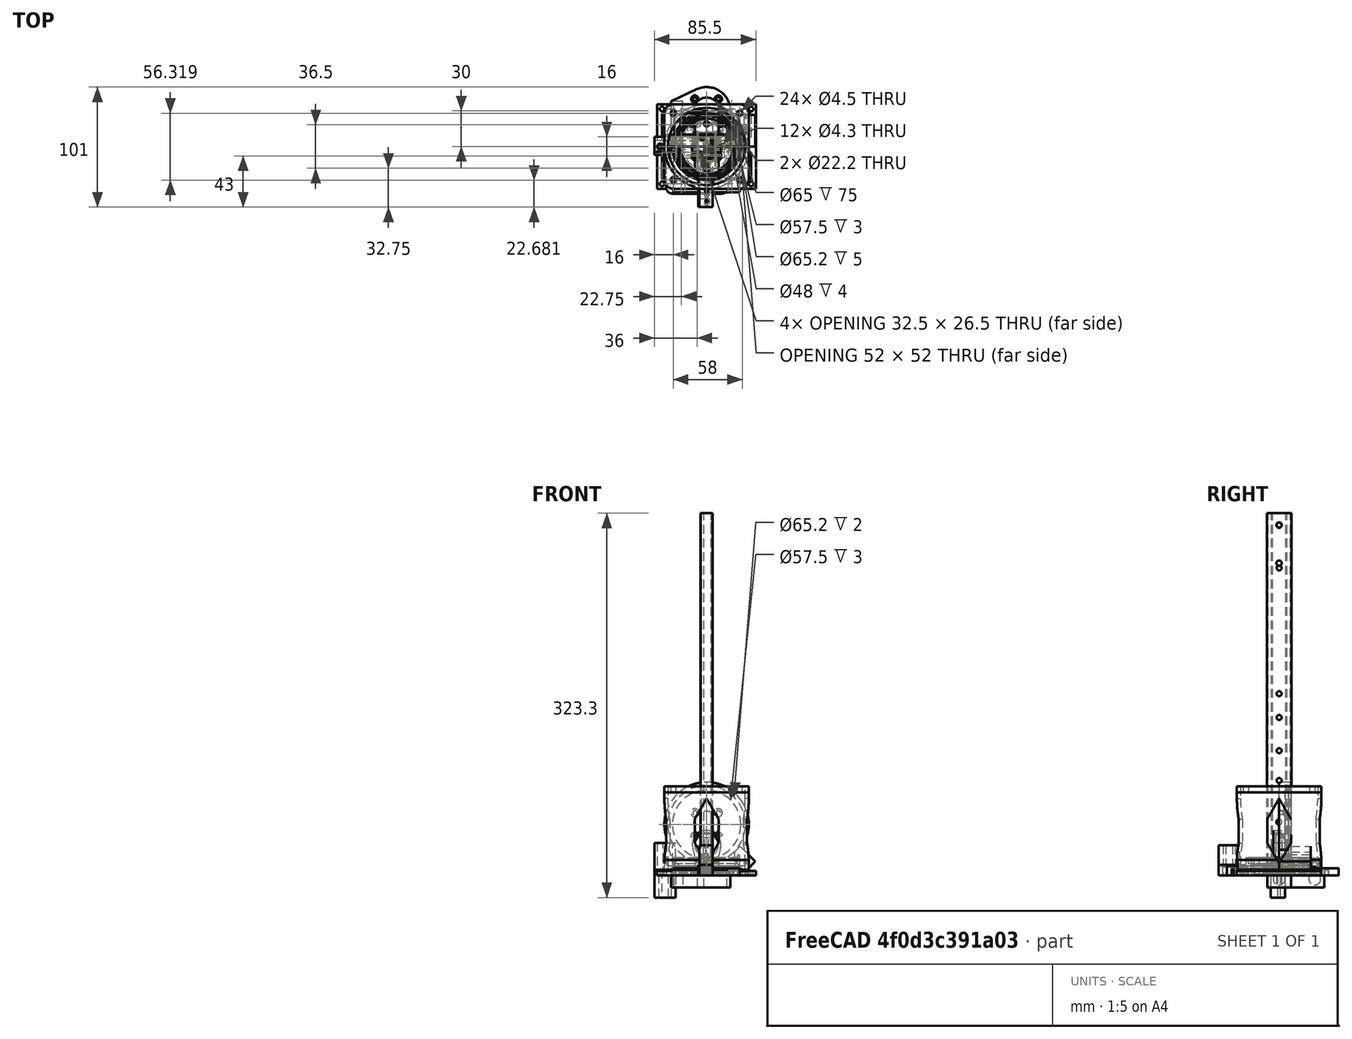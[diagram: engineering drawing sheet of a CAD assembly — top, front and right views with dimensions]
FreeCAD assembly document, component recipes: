
FREECAD ASSEMBLY — COMPONENT RECIPES ("A4")

This assembly document has 19 components, labeled P0..P18 below (a component is one placed body or linked part). 19 of them carry a construction recipe — the FreeCAD feature program that regenerates the part from scratch, quoted from this document or its linked companion documents; the rest are supplied as boundary geometry only. No exploded tour is included for this assembly.
COMPONENT P0 — recipe-attached ("J2_CABLE_GUIDE_1V0", modeled in this document).
Construction recipe (the document's own serialized feature program — sketch geometry with constraints, then the solid features built on it; lengths are millimeters unless a unit is written):

FEATURE [PartDesign::CoordinateSystem] LCS_0012
  AttacherType = Attacher::AttachEngine3D
  MapMode = 2
  Support = -> [X_Axis032]
FEATURE [Sketcher::SketchObject] Sketch067
  FullyConstrained = true
  MapMode = 5
  Support = -> [XY_Plane032]
  sketch-geometry (6):
    g0: Circle CenterX=0 CenterY=19 CenterZ=0 NormalX=0 NormalY=0 NormalZ=1 AngleXU=0 Radius=2.25
    g1: Circle CenterX=0 CenterY=-19 CenterZ=0 NormalX=0 NormalY=0 NormalZ=1 AngleXU=0 Radius=2.25
    g2: ArcOfCircle CenterX=0 CenterY=0 CenterZ=0 NormalX=0 NormalY=0 NormalZ=1 AngleXU=0 Radius=23.5 StartAngle=1.13125 EndAngle=2.01035
    g3: ArcOfCircle CenterX=0 CenterY=0 CenterZ=0 NormalX=0 NormalY=0 NormalZ=1 AngleXU=0 Radius=23.5 StartAngle=4.27284 EndAngle=5.15194
    g4: LineSegment StartX=-10 StartY=21.2662 StartZ=0 EndX=-10 EndY=-21.2662 EndZ=0
    g5: LineSegment StartX=10 StartY=-21.2662 StartZ=0 EndX=10 EndY=21.2662 EndZ=0
  constraints (16):
    c: PointOnObject(g0,g-2)
    c: Diameter(g1) = 4.5
    c: Equal(g1,g0)
    c: DistanceY(g1,g0) = 38
    c: Symmetric(g0,g1,g-1)
    c: Coincident(g2,g-1)
    c: Coincident(g3,g2)
    c: Coincident(g4,g3)
    c: Coincident(g5,g3)
    c: Coincident(g5,g2)
    c: Coincident(g2,g4)
    c: Vertical(g4)
    c: Symmetric(g2,g3,g-1)
    c: Horizontal(g2,g2)
    c: DistanceX(g2,g2) = 20
    c: Diameter(g2) = 47
FEATURE [PartDesign::Pad] Pad043
  Direction = (1,1,1)
  Length = 15
  Length2 = 100
  Profile = -> Sketch067
  Type = 0
FEATURE [Sketcher::SketchObject] Sketch068
  FullyConstrained = true
  MapMode = 5
  Placement = pos=(0,0,0) rot=(1,0,0;1.5708rad)
  Support = -> [XZ_Plane032]
  sketch-geometry (5):
    g0: Circle CenterX=0 CenterY=26 CenterZ=0 NormalX=0 NormalY=0 NormalZ=1 AngleXU=0 Radius=10
    g1: ArcOfCircle CenterX=0 CenterY=26 CenterZ=0 NormalX=0 NormalY=0 NormalZ=1 AngleXU=0 Radius=12 StartAngle=6.08159 EndAngle=9.62637
    g2: LineSegment StartX=-11.757 StartY=23.5973 StartZ=0 EndX=-10 EndY=15 EndZ=0
    g3: LineSegment StartX=11.757 StartY=23.5973 StartZ=0 EndX=10 EndY=15 EndZ=0
    g4: LineSegment StartX=10 StartY=15 StartZ=0 EndX=-10 EndY=15 EndZ=0
  constraints (12):
    c: PointOnObject(g0,g-2)
    c: Diameter(g0) = 20
    c: Coincident(g1,g0)
    c: Coincident(g4,g3)
    c: Coincident(g4,g2)
    c: Symmetric(g2,g3,g-2)
    c: DistanceX(g4,g4) = 20
    c: DistanceY(g-1,g3) = 15
    c: Diameter(g1) = 24
    c: DistanceY(g-1,g0) = 26
    c: Tangent(g2,g1) = -1.5708
    c: Tangent(g3,g1) = 1.5708
FEATURE [PartDesign::Pad] Pad044
  BaseFeature = -> Pad043
  Direction = (1,1,1)
  Length = 10
  Length2 = 100
  Midplane = true
  Profile = -> Sketch068
  Type = 0
FEATURE [Sketcher::SketchObject] Sketch069
  FullyConstrained = true
  MapMode = 5
  Placement = pos=(0,0,0) rot=(0.57735,0.57735,0.57735;2.0944rad)
  Support = -> [YZ_Plane032]
  expr: Constraints[9] = <<var>>.humerusW + 2
  sketch-geometry (4):
    g0: LineSegment StartX=-11.3187 StartY=0 StartZ=0 EndX=11.3187 EndY=0 EndZ=0
    g1: LineSegment StartX=11.3187 StartY=0 StartZ=0 EndX=11.3187 EndY=11 EndZ=0
    g2: LineSegment StartX=11.3187 StartY=11 StartZ=0 EndX=-11.3187 EndY=11 EndZ=0
    g3: LineSegment StartX=-11.3187 StartY=11 StartZ=0 EndX=-11.3187 EndY=0 EndZ=0
  constraints (11):
    c: Coincident(g0,g1)
    c: Coincident(g1,g2)
    c: Coincident(g2,g3)
    c: Coincident(g3,g0)
    c: Horizontal(g0)
    c: Vertical(g1)
    c: Vertical(g3)
    c: PointOnObject(g0,g-1)
    c: Symmetric(g2,g1,g-2)
    c: DistanceX(g2,g2) = 22.6375
    c: DistanceY(g1,g1) = 11
FEATURE [PartDesign::Pocket] Pocket022
  BaseFeature = -> Pad044
  Length = 5
  Length2 = 100
  Midplane = true
  Profile = -> Sketch069
  Type = 1
FEATURE [PartDesign::Body] J2_CABLE_GUIDE_1_0  label="Body008"
  Group = -> [LCS_0012,Sketch067,Pad043,Sketch068,Pad044,Sketch069,Pocket022]
  Origin = -> Origin032
  Tip = -> Pocket022
COMPONENT P1 — recipe-attached ("J0_BASE_2V0", modeled in this document).
Construction recipe (the document's own serialized feature program — sketch geometry with constraints, then the solid features built on it; lengths are millimeters unless a unit is written):

FEATURE [Sketcher::SketchObject] Sketch004
  FullyConstrained = true
  MapMode = 5
  Support = -> [XY_Plane004]
  expr: Constraints[46] = <<var>>.motorJ0HoleD
  expr: Constraints[41] = <<var>>.motorJ0LocD
  expr: Constraints[40] = <<var>>.motorJ0HolePD
  expr: Constraints[24] = <<var>>.riserOD
  expr: Constraints[20] = <<var>>.riserOD - 15
  expr: Constraints[16] = <<var>>.riserHoleD
  sketch-geometry (22):
    g0: LineSegment StartX=-28 StartY=35.5 StartZ=0 EndX=28 EndY=35.5 EndZ=0
    g1: LineSegment StartX=35.5 StartY=28 StartZ=0 EndX=35.5 EndY=-28 EndZ=0
    g2: LineSegment StartX=28 StartY=-35.5 StartZ=0 EndX=-28 EndY=-35.5 EndZ=0
    g3: LineSegment StartX=-35.5 StartY=-28 StartZ=0 EndX=-35.5 EndY=28 EndZ=0
    g4: ArcOfCircle CenterX=-28 CenterY=28 CenterZ=0 NormalX=0 NormalY=0 NormalZ=1 AngleXU=0 Radius=7.5 StartAngle=1.5708 EndAngle=3.14159
    g5: ArcOfCircle CenterX=-28 CenterY=-28 CenterZ=0 NormalX=0 NormalY=0 NormalZ=1 AngleXU=0 Radius=7.5 StartAngle=3.14159 EndAngle=4.71239
    g6: ArcOfCircle CenterX=28 CenterY=-28 CenterZ=0 NormalX=0 NormalY=0 NormalZ=1 AngleXU=0 Radius=7.5 StartAngle=4.71239 EndAngle=6.28319
    g7: ArcOfCircle CenterX=28 CenterY=28 CenterZ=0 NormalX=0 NormalY=0 NormalZ=1 AngleXU=0 Radius=7.5 StartAngle=-9e-16 EndAngle=1.5708
    g8: Circle CenterX=-28 CenterY=28 CenterZ=0 NormalX=0 NormalY=0 NormalZ=1 AngleXU=0 Radius=2.25
    g9: Circle CenterX=28 CenterY=28 CenterZ=0 NormalX=0 NormalY=0 NormalZ=1 AngleXU=0 Radius=2.25
    g10: Circle CenterX=28 CenterY=-28 CenterZ=0 NormalX=0 NormalY=0 NormalZ=1 AngleXU=0 Radius=2.25
    g11: Circle CenterX=-28 CenterY=-28 CenterZ=0 NormalX=0 NormalY=0 NormalZ=1 AngleXU=0 Radius=2.25
    g12: Circle CenterX=0 CenterY=0 CenterZ=0 NormalX=0 NormalY=0 NormalZ=1 AngleXU=0 Radius=11.1
    g13: LineSegment StartX=-9.89949 StartY=9.89949 StartZ=0 EndX=9.89949 EndY=9.89949 EndZ=0
    g14: LineSegment StartX=9.89949 StartY=9.89949 StartZ=0 EndX=9.89949 EndY=-9.89949 EndZ=0
    g15: LineSegment StartX=9.89949 StartY=-9.89949 StartZ=0 EndX=-9.89949 EndY=-9.89949 EndZ=0
    g16: LineSegment StartX=-9.89949 StartY=-9.89949 StartZ=0 EndX=-9.89949 EndY=9.89949 EndZ=0
    g17: Circle CenterX=0 CenterY=0 CenterZ=0 NormalX=0 NormalY=0 NormalZ=1 AngleXU=0 Radius=14
    g18: Circle CenterX=-9.89949 CenterY=9.89949 CenterZ=0 NormalX=0 NormalY=0 NormalZ=1 AngleXU=0 Radius=1.65
    g19: Circle CenterX=9.89949 CenterY=9.89949 CenterZ=0 NormalX=0 NormalY=0 NormalZ=1 AngleXU=0 Radius=1.65
    g20: Circle CenterX=9.89949 CenterY=-9.89949 CenterZ=0 NormalX=0 NormalY=0 NormalZ=1 AngleXU=0 Radius=1.65
    g21: Circle CenterX=-9.89949 CenterY=-9.89949 CenterZ=0 NormalX=0 NormalY=0 NormalZ=1 AngleXU=0 Radius=1.65
  constraints (50):
    c: Horizontal(g0)
    c: Horizontal(g2)
    c: Vertical(g1)
    c: Vertical(g3)
    c: Tangent(g0,g4) = 1.5708
    c: Tangent(g3,g4) = 1.5708
    c: Tangent(g3,g5) = 1.5708
    c: Tangent(g2,g5) = 1.5708
    c: Tangent(g2,g6) = 1.5708
    c: Tangent(g1,g6) = 1.5708
    c: Tangent(g1,g7) = 1.5708
    c: Tangent(g0,g7) = 1.5708
    c: Coincident(g8,g4)
    c: Coincident(g9,g7)
    c: Coincident(g10,g6)
    c: Coincident(g11,g5)
    c: Diameter(g11) = 4.5
    c: Equal(g11,g8)
    c: Equal(g11,g9)
    c: Equal(g11,g10)
    c: DistanceX(g4,g7) = 56
    c: Symmetric(g4,g5,g-1)
    c: Symmetric(g4,g7,g-2)
    c: Equal(g0,g3)
    c: DistanceX(g3,g1) = 71
    c: Equal(g6,g7)
    c: Coincident(g12,g-1)
    c: Coincident(g13,g14)
    c: Coincident(g14,g15)
    c: Coincident(g15,g16)
    c: Coincident(g16,g13)
    c: Horizontal(g13)
    c: Horizontal(g15)
    c: Vertical(g14)
    c: Vertical(g16)
    c: Coincident(g17,g12)
    c: PointOnObject(g13,g17)
    c: PointOnObject(g13,g17)
    c: Equal(g14,g15)
    c: PointOnObject(g14,g17)
    c: Diameter(g17) = 28
    c: Diameter(g12) = 22.2
    c: Coincident(g18,g13)
    c: Coincident(g19,g13)
    c: Coincident(g20,g14)
    c: Coincident(g21,g15)
    c: Diameter(g21) = 3.3
    c: Equal(g21,g20)
    c: Equal(g21,g19)
    c: Equal(g21,g18)
FEATURE [PartDesign::Pad] Pad005
  Direction = (1,1,1)
  Length = 5
  Length2 = 100
  Profile = -> Sketch004
  Refine = true
  Type = 0
FEATURE [Sketcher::SketchObject] Sketch005
  AttachmentOffset = pos=(0,0,5) rot=(0,0,1;0rad)
  FullyConstrained = true
  MapMode = 5
  Placement = pos=(0,0,5) rot=(0,0,1;0rad)
  Support = -> [XY_Plane004]
  expr: .AttachmentOffset.Base.z = 5
  sketch-geometry (2):
    g0: Circle CenterX=0 CenterY=0 CenterZ=0 NormalX=0 NormalY=0 NormalZ=1 AngleXU=0 Radius=35.5
    g1: Circle CenterX=0 CenterY=0 CenterZ=0 NormalX=0 NormalY=0 NormalZ=1 AngleXU=0 Radius=32.6
  constraints (4):
    c: Coincident(g0,g-1)
    c: Coincident(g1,g0)
    c: Diameter(g1) = 65.2
    c: Diameter(g0) = 71
FEATURE [PartDesign::Pad] Pad006
  BaseFeature = -> Pad005
  Direction = (1,1,1)
  Length = 8
  Length2 = 100
  Profile = -> Sketch005
  Refine = true
  Type = 0
FEATURE [Sketcher::SketchObject] Sketch070
  AttachmentOffset = pos=(0,0,5) rot=(0,0,1;0rad)
  FullyConstrained = true
  MapMode = 5
  Placement = pos=(0,0,5) rot=(0,0,1;0rad)
  Support = -> [XY_Plane004]
  expr: .AttachmentOffset.Base.z = 5
  sketch-geometry (2):
    g0: Circle CenterX=0 CenterY=0 CenterZ=0 NormalX=0 NormalY=0 NormalZ=1 AngleXU=0 Radius=28.75
    g1: Circle CenterX=0 CenterY=0 CenterZ=0 NormalX=0 NormalY=0 NormalZ=1 AngleXU=0 Radius=32.6
  constraints (4):
    c: Coincident(g0,g-1)
    c: Coincident(g1,g0)
    c: Diameter(g1) = 65.2
    c: Diameter(g0) = 57.5
FEATURE [PartDesign::Pad] Pad045
  BaseFeature = -> Pad006
  Direction = (1,1,1)
  Length = 3
  Length2 = 100
  Profile = -> Sketch070
  Refine = true
  Type = 0
FEATURE [Sketcher::SketchObject] Sketch071
  FullyConstrained = true
  MapMode = 5
  Support = -> [XY_Plane004]
  sketch-geometry (7):
    g0: LineSegment StartX=-6 StartY=-33 StartZ=0 EndX=5 EndY=-33 EndZ=0
    g1: LineSegment StartX=5 StartY=-33 StartZ=0 EndX=5 EndY=-51 EndZ=0
    g2: LineSegment StartX=5 StartY=-51 StartZ=0 EndX=-6 EndY=-51 EndZ=0
    g3: LineSegment StartX=-6 StartY=-51 StartZ=0 EndX=-6 EndY=-33 EndZ=0
    g4: Circle CenterX=0 CenterY=0 CenterZ=0 NormalX=0 NormalY=0 NormalZ=1 AngleXU=0 Radius=33
    g5: Circle CenterX=0 CenterY=-38 CenterZ=0 NormalX=0 NormalY=0 NormalZ=1 AngleXU=0 Radius=1.0922
    g6: Circle CenterX=0 CenterY=-46 CenterZ=0 NormalX=0 NormalY=0 NormalZ=1 AngleXU=0 Radius=1.0922
  constraints (21):
    c: Coincident(g0,g1)
    c: Coincident(g1,g2)
    c: Coincident(g2,g3)
    c: Coincident(g3,g0)
    c: Horizontal(g0)
    c: Vertical(g1)
    c: Vertical(g3)
    c: DistanceY(g1,g1) = 18
    c: Coincident(g4,g-1)
    c: Diameter(g4) = 66
    c: Tangent(g0,g4)
    c: PointOnObject(g5,g-2)
    c: PointOnObject(g6,g-2)
    c: Diameter(g6) = 2.1844
    c: Equal(g6,g5)
    c: DistanceY(g6,g5) = 8
    c: DistanceY(g5,g0) = 5
    c: DistanceY(g1,g6) = 5
    c: DistanceX(g-1,g1) = 5
    c: DistanceX(g2,g-1) = 6
    c: Horizontal(g2)
FEATURE [PartDesign::Pad] Pad046
  BaseFeature = -> Pad045
  Direction = (1,1,1)
  Length = 25.5
  Length2 = 100
  Profile = -> Sketch071
  Type = 0
  expr: Length = Variables.encoderJ0H
FEATURE [Sketcher::SketchObject] Sketch079
  AttachmentOffset = pos=(0,0,5) rot=(0,0,1;0rad)
  FullyConstrained = true
  MapMode = 5
  Placement = pos=(0,0,5) rot=(0,0,1;0rad)
  Support = -> [XY_Plane004]
  sketch-geometry (9):
    g0: Circle CenterX=0 CenterY=0 CenterZ=0 NormalX=0 NormalY=0 NormalZ=1 AngleXU=0 Radius=14
    g1: LineSegment StartX=-9.89949 StartY=9.89949 StartZ=0 EndX=9.89949 EndY=9.89949 EndZ=0
    g2: LineSegment StartX=9.89949 StartY=9.89949 StartZ=0 EndX=9.89949 EndY=-9.89949 EndZ=0
    g3: LineSegment StartX=9.89949 StartY=-9.89949 StartZ=0 EndX=-9.89949 EndY=-9.89949 EndZ=0
    g4: LineSegment StartX=-9.89949 StartY=-9.89949 StartZ=0 EndX=-9.89949 EndY=9.89949 EndZ=0
    g5: Circle CenterX=-9.89949 CenterY=9.89949 CenterZ=0 NormalX=0 NormalY=0 NormalZ=1 AngleXU=0 Radius=1.5
    g6: Circle CenterX=9.89949 CenterY=9.89949 CenterZ=0 NormalX=0 NormalY=0 NormalZ=1 AngleXU=0 Radius=1.5
    g7: Circle CenterX=9.89949 CenterY=-9.89949 CenterZ=0 NormalX=0 NormalY=0 NormalZ=1 AngleXU=0 Radius=1.5
    g8: Circle CenterX=-9.89949 CenterY=-9.89949 CenterZ=0 NormalX=0 NormalY=0 NormalZ=1 AngleXU=0 Radius=1.5
  constraints (22):
    c: Coincident(g0,g-1)
    c: Coincident(g1,g2)
    c: Coincident(g2,g3)
    c: Coincident(g3,g4)
    c: Coincident(g4,g1)
    c: Horizontal(g1)
    c: Horizontal(g3)
    c: Vertical(g2)
    c: Vertical(g4)
    c: PointOnObject(g1,g0)
    c: PointOnObject(g2,g0)
    c: PointOnObject(g1,g0)
    c: Equal(g1,g4)
    c: Diameter(g0) = 28
    c: Coincident(g5,g1)
    c: Coincident(g6,g1)
    c: Coincident(g7,g2)
    c: Coincident(g8,g3)
    c: Diameter(g8) = 3
    c: Equal(g8,g7)
    c: Equal(g8,g6)
    c: Equal(g8,g5)
FEATURE [PartDesign::Hole] Hole002
  BaseFeature = -> Pad046
  Depth = 25
  DepthType = 1
  Diameter = 3.4
  DrillForDepth = false
  DrillPoint = 1
  DrillPointAngle = 118
  HoleCutCountersinkAngle = 90
  HoleCutCustomValues = false
  HoleCutDepth = 0
  HoleCutDiameter = 6.7
  HoleCutType = 7
  ModelActualThread = false
  Profile = -> Sketch079
  Tapered = false
  TaperedAngle = 90
  ThreadAngle = 0
  ThreadClass = 0
  ThreadCutOffInner = 0
  ThreadCutOffOuter = 0
  ThreadDirection = 0
  ThreadFit = 0
  ThreadPitch = 0
  ThreadSize = 9
  ThreadType = 1
  Threaded = false
FEATURE [PartDesign::Body] Body001
  Group = -> [Sketch004,Pad005,Sketch005,Pad006,Sketch070,Pad045,Sketch071,Pad046,Sketch079,Hole002]
  Origin = -> Origin004
  Tip = -> Hole002
COMPONENT P2 — recipe-attached ("J1_BASE_2V0", modeled in this document).
Construction recipe (the document's own serialized feature program — sketch geometry with constraints, then the solid features built on it; lengths are millimeters unless a unit is written):

FEATURE [Sketcher::SketchObject] Sketch016
  FullyConstrained = true
  MapMode = 5
  Support = -> [XY_Plane008]
  sketch-geometry (7):
    g0: LineSegment StartX=-20 StartY=15 StartZ=0 EndX=20 EndY=15 EndZ=0
    g1: Circle CenterX=-20 CenterY=15 CenterZ=0 NormalX=0 NormalY=0 NormalZ=1 AngleXU=0 Radius=2.35
    g2: Circle CenterX=20 CenterY=15 CenterZ=0 NormalX=0 NormalY=0 NormalZ=1 AngleXU=0 Radius=2.35
    g3: LineSegment StartX=-27 StartY=0 StartZ=0 EndX=27 EndY=0 EndZ=0
    g4: LineSegment StartX=27 StartY=0 StartZ=0 EndX=27 EndY=20 EndZ=0
    g5: LineSegment StartX=27 StartY=20 StartZ=0 EndX=-27 EndY=20 EndZ=0
    g6: LineSegment StartX=-27 StartY=20 StartZ=0 EndX=-27 EndY=0 EndZ=0
  constraints (18):
    c: Coincident(g1,g0)
    c: Coincident(g2,g0)
    c: DistanceX(g0,g0) = 40
    c: DistanceY(g-1,g2) = 15
    c: Symmetric(g1,g2,g-2)
    c: Coincident(g4,g5)
    c: Coincident(g5,g6)
    c: Coincident(g6,g3)
    c: Horizontal(g3)
    c: Vertical(g4)
    c: Vertical(g6)
    c: PointOnObject(g3,g-1)
    c: DistanceX(g5,g5) = 54
    c: Symmetric(g5,g4,g-2)
    c: DistanceY(g4,g4) = 20
    c: Coincident(g3,g4)
    c: Diameter(g2) = 4.7
    c: Equal(g2,g1)
FEATURE [PartDesign::Pad] Pad010
  AllowMultiFace = false
  Direction = (1,1,1)
  Length = 5
  Length2 = 100
  Profile = -> Sketch016
  Type = 0
FEATURE [Sketcher::SketchObject] Sketch017
  AttachmentOffset = pos=(0,0,-5) rot=(0,0,1;0rad)
  FullyConstrained = true
  MapMode = 5
  Placement = pos=(0,5,1.1e-15) rot=(1,0,0;1.5708rad)
  Support = -> [XZ_Plane008]
  expr: Constraints[1] = <<var>>.baseJ1MotorH
  sketch-geometry (1):
    g0: Circle CenterX=0 CenterY=43 CenterZ=0 NormalX=0 NormalY=0 NormalZ=1 AngleXU=0 Radius=32.6
  constraints (3):
    c: Diameter(g0) = 65.2
    c: DistanceY(g-1,g0) = 43
    c: PointOnObject(g0,g-2)
FEATURE [Sketcher::SketchObject] Sketch019
  FullyConstrained = true
  MapMode = 5
  Placement = pos=(0,0,0) rot=(1,0,0;1.5708rad)
  Support = -> [XZ_Plane008]
  expr: Constraints[3] = <<var>>.baseJ1MotorH
  expr: Constraints[32] = <<var>>.motorJ0HolePD
  expr: Constraints[23] = <<var>>.motorJ0LocD
  expr: Constraints[18] = <<var>>.motorJ0HoleD
  sketch-geometry (15):
    g0: LineSegment StartX=-27 StartY=5 StartZ=0 EndX=-34.4144 EndY=34.2878 EndZ=0
    g1: LineSegment StartX=34.4144 StartY=34.2878 StartZ=0 EndX=27 EndY=5 EndZ=0
    g2: LineSegment StartX=-27 StartY=5 StartZ=0 EndX=27 EndY=5 EndZ=0
    g3: ArcOfCircle CenterX=0 CenterY=43 CenterZ=0 NormalX=0 NormalY=0 NormalZ=1 AngleXU=0 Radius=35.5 StartAngle=6.03524 EndAngle=9.67272
    g4: Circle CenterX=0 CenterY=43 CenterZ=0 NormalX=0 NormalY=0 NormalZ=1 AngleXU=0 Radius=11.1
    g5: Circle CenterX=9.89949 CenterY=52.8995 CenterZ=0 NormalX=0 NormalY=0 NormalZ=1 AngleXU=0 Radius=1.65
    g6: Circle CenterX=-9.89949 CenterY=52.8995 CenterZ=0 NormalX=0 NormalY=0 NormalZ=1 AngleXU=0 Radius=1.65
    g7: Circle CenterX=9.89949 CenterY=33.1005 CenterZ=0 NormalX=0 NormalY=0 NormalZ=1 AngleXU=0 Radius=1.65
    g8: Circle CenterX=-9.89949 CenterY=33.1005 CenterZ=0 NormalX=0 NormalY=0 NormalZ=1 AngleXU=0 Radius=1.65
    g9: LineSegment StartX=-9.89949 StartY=52.8995 StartZ=0 EndX=9.89949 EndY=52.8995 EndZ=0
    g10: LineSegment StartX=9.89949 StartY=52.8995 StartZ=0 EndX=9.89949 EndY=33.1005 EndZ=0
    g11: LineSegment StartX=9.89949 StartY=33.1005 StartZ=0 EndX=-9.89949 EndY=33.1005 EndZ=0
    g12: LineSegment StartX=-9.89949 StartY=33.1005 StartZ=0 EndX=-9.89949 EndY=52.8995 EndZ=0
    g13: LineSegment StartX=-11.1 StartY=43 StartZ=0 EndX=11.1 EndY=43 EndZ=0
    g14: Circle CenterX=0 CenterY=43 CenterZ=0 NormalX=0 NormalY=0 NormalZ=1 AngleXU=0 Radius=14
  constraints (36):
    c: Coincident(g2,g0)
    c: Coincident(g2,g1)
    c: PointOnObject(g3,g-2)
    c: DistanceY(g-1,g3) = 43
    c: Tangent(g3,g0) = 1.5708
    c: Tangent(g3,g1) = 1.5708
    c: Coincident(g4,g3)
    c: Coincident(g9,g10)
    c: Coincident(g10,g11)
    c: Coincident(g11,g12)
    c: Coincident(g12,g9)
    c: Horizontal(g11)
    c: Vertical(g10)
    c: Vertical(g12)
    c: Coincident(g9,g6)
    c: Coincident(g10,g7)
    c: Coincident(g5,g9)
    c: Coincident(g11,g8)
    c: Diameter(g5) = 3.3
    c: Equal(g5,g7)
    c: Equal(g5,g6)
    c: Equal(g5,g8)
    c: Equal(g10,g9)
    c: Diameter(g4) = 22.2
    c: Symmetric(g6,g5,g-2)
    c: PointOnObject(g3,g13)
    c: Symmetric(g6,g8,g13)
    c: PointOnObject(g13,g4)
    c: PointOnObject(g13,g4)
    c: Symmetric(g0,g1,g-2)
    c: Coincident(g14,g3)
    c: PointOnObject(g5,g14)
    c: Diameter(g14) = 28
    c: Diameter(g3) = 71
    c: DistanceX(g2,g2) = 54
    c: DistanceY(g-1,g0) = 5
FEATURE [PartDesign::Pad] Pad009
  AllowMultiFace = false
  BaseFeature = -> Pad010
  Direction = (1,1,1)
  Length = 10
  Length2 = 8.5
  Profile = -> Sketch019
  Reversed = true
  Type = 0
FEATURE [PartDesign::Pocket] Pocket006
  AllowMultiFace = false
  BaseFeature = -> Pad009
  Length = 5
  Length2 = 100
  Profile = -> Sketch017
  Type = 1
FEATURE [Sketcher::SketchObject] Sketch076
  AttachmentOffset = pos=(0,0,-4) rot=(0,0,1;0rad)
  FullyConstrained = true
  MapMode = 5
  Placement = pos=(0,4,9e-16) rot=(1,0,0;1.5708rad)
  Support = -> [XZ_Plane008]
  expr: Constraints[3] = Variables.baseJ1MotorH
  sketch-geometry (2):
    g0: Circle CenterX=0 CenterY=43 CenterZ=0 NormalX=0 NormalY=0 NormalZ=1 AngleXU=0 Radius=28.75
    g1: Circle CenterX=0 CenterY=43 CenterZ=0 NormalX=0 NormalY=0 NormalZ=1 AngleXU=0 Radius=32.6
  constraints (5):
    c: PointOnObject(g0,g-2)
    c: Coincident(g1,g0)
    c: Diameter(g1) = 65.2
    c: DistanceY(g-1,g0) = 43
    c: Diameter(g0) = 57.5
FEATURE [PartDesign::Pad] Pad049
  BaseFeature = -> Pocket006
  Direction = (1,1,1)
  Length = 4
  Length2 = 100
  Profile = -> Sketch076
  Reversed = true
  Type = 0
FEATURE [Sketcher::SketchObject] Sketch090
  FullyConstrained = true
  MapMode = 5
  Placement = pos=(0,0,0) rot=(1,0,0;1.5708rad)
  Support = -> [XZ_Plane008]
  sketch-geometry (10):
    g0: Circle CenterX=0 CenterY=43 CenterZ=0 NormalX=0 NormalY=0 NormalZ=1 AngleXU=0 Radius=33
    g1: LineSegment StartX=28.2843 StartY=24.6152 StartZ=0 EndX=23.3345 EndY=19.6655 EndZ=0
    g2: LineSegment StartX=23.3345 StartY=12.5944 StartZ=0 EndX=32.5269 EndY=3.40202 EndZ=0
    g3: LineSegment StartX=32.5269 StartY=3.40202 StartZ=0 EndX=41.0122 EndY=11.8873 EndZ=0
    g4: LineSegment StartX=41.0122 StartY=11.8873 StartZ=0 EndX=28.2843 EndY=24.6152 EndZ=0
    g5: Circle CenterX=32.5269 CenterY=10.4731 CenterZ=0 NormalX=0 NormalY=0 NormalZ=1 AngleXU=0 Radius=1.092
    g6: Circle CenterX=26.8701 CenterY=16.1299 CenterZ=0 NormalX=0 NormalY=0 NormalZ=1 AngleXU=0 Radius=1.092
    g7: LineSegment StartX=23.3345 StartY=19.6655 StartZ=0 EndX=36.0624 EndY=6.93755 EndZ=0
    g8: LineSegment StartX=0 StartY=43 StartZ=0 EndX=36.0624 EndY=6.93755 EndZ=0
    g9: LineSegment StartX=23.3345 StartY=12.5944 StartZ=0 EndX=23.3345 EndY=19.6655 EndZ=0
  constraints (29):
    c: PointOnObject(g0,g-2)
    c: Diameter(g0) = 66
    c: DistanceY(g-1,g0) = 43
    c: Coincident(g2,g3)
    c: Coincident(g3,g4)
    c: Coincident(g4,g1)
    c: Parallel(g4,g2)
    c: Parallel(g1,g3)
    c: Perpendicular(g3,g4)
    c: Distance(g4) = 18
    c: PointOnObject(g7,g1)
    c: PointOnObject(g7,g3)
    c: Parallel(g7,g4)
    c: PointOnObject(g6,g7)
    c: PointOnObject(g5,g7)
    c: Distance(g5,g7) = 5
    c: Distance(g6,g5) = 8
    c: Diameter(g5) = 2.184
    c: Equal(g5,g6)
    c: Distance(g7,g3) = 7
    c: Angle(g2,g-1) = 0.785398
    c: Coincident(g8,g0)
    c: Coincident(g8,g7)
    c: PointOnObject(g7,g8)
    c: Distance(g7,g2) = 5
    c: Vertical(g9)
    c: Coincident(g9,g7)
    c: Coincident(g2,g9)
    c: Tangent(g1,g0) = 1.5708
FEATURE [PartDesign::Pad] Pad055
  BaseFeature = -> Pad049
  Direction = (1,1,1)
  Length = 26.5
  Length2 = 100
  Profile = -> Sketch090
  Refine = true
  Reversed = true
  Type = 0
  expr: Length = <<var>>.baseJ1EncoderH
FEATURE [Sketcher::SketchObject] Sketch110
  AttachmentOffset = pos=(0,0,-5) rot=(0,0,1;0rad)
  FullyConstrained = true
  MapMode = 5
  Placement = pos=(0,5,1.1e-15) rot=(1,0,0;1.5708rad)
  Support = -> [XZ_Plane008]
  sketch-geometry (9):
    g0: Circle CenterX=0 CenterY=43 CenterZ=0 NormalX=0 NormalY=0 NormalZ=1 AngleXU=0 Radius=14
    g1: LineSegment StartX=-9.89949 StartY=52.8995 StartZ=0 EndX=9.89949 EndY=52.8995 EndZ=0
    g2: LineSegment StartX=9.89949 StartY=52.8995 StartZ=0 EndX=9.89949 EndY=33.1005 EndZ=0
    g3: LineSegment StartX=9.89949 StartY=33.1005 StartZ=0 EndX=-9.89949 EndY=33.1005 EndZ=0
    g4: LineSegment StartX=-9.89949 StartY=33.1005 StartZ=0 EndX=-9.89949 EndY=52.8995 EndZ=0
    g5: Circle CenterX=-9.89949 CenterY=52.8995 CenterZ=0 NormalX=0 NormalY=0 NormalZ=1 AngleXU=0 Radius=1.5
    g6: Circle CenterX=9.89949 CenterY=52.8995 CenterZ=0 NormalX=0 NormalY=0 NormalZ=1 AngleXU=0 Radius=1.5
    g7: Circle CenterX=9.89949 CenterY=33.1005 CenterZ=0 NormalX=0 NormalY=0 NormalZ=1 AngleXU=0 Radius=1.5
    g8: Circle CenterX=-9.89949 CenterY=33.1005 CenterZ=0 NormalX=0 NormalY=0 NormalZ=1 AngleXU=0 Radius=1.5
  constraints (23):
    c: Coincident(g1,g2)
    c: Coincident(g2,g3)
    c: Coincident(g3,g4)
    c: Coincident(g4,g1)
    c: Horizontal(g1)
    c: Horizontal(g3)
    c: Vertical(g2)
    c: Vertical(g4)
    c: PointOnObject(g1,g0)
    c: PointOnObject(g2,g0)
    c: PointOnObject(g1,g0)
    c: Equal(g1,g4)
    c: Diameter(g0) = 28
    c: Coincident(g5,g1)
    c: Coincident(g6,g1)
    c: Coincident(g7,g2)
    c: Coincident(g8,g3)
    c: Diameter(g8) = 3
    c: Equal(g8,g7)
    c: Equal(g8,g6)
    c: Equal(g8,g5)
    c: PointOnObject(g0,g-2)
    c: DistanceY(g-1,g0) = 43
FEATURE [PartDesign::Hole] Hole009
  BaseFeature = -> Pad055
  Depth = 25
  DepthType = 1
  Diameter = 3.4
  DrillForDepth = false
  DrillPoint = 1
  DrillPointAngle = 118
  HoleCutCountersinkAngle = 90
  HoleCutCustomValues = false
  HoleCutDepth = 0
  HoleCutDiameter = 6.7
  HoleCutType = 7
  ModelActualThread = false
  Profile = -> Sketch110
  Refine = true
  Reversed = true
  Tapered = false
  TaperedAngle = 90
  ThreadAngle = 0
  ThreadClass = 0
  ThreadCutOffInner = 0
  ThreadCutOffOuter = 0
  ThreadDirection = 0
  ThreadFit = 0
  ThreadPitch = 0
  ThreadSize = 9
  ThreadType = 1
  Threaded = false
FEATURE [PartDesign::Body] Body003
  Group = -> [Sketch016,Pad010,Sketch019,Pad009,Sketch017,Pocket006,Sketch076,Pad049,Sketch090,Pad055,Sketch110,Hole009]
  Origin = -> Origin008
  Tip = -> Hole009
COMPONENT P3 — recipe-attached ("J2_BASE_2V0", modeled in this document).
Construction recipe (the document's own serialized feature program — sketch geometry with constraints, then the solid features built on it; lengths are millimeters unless a unit is written):

FEATURE [Sketcher::SketchObject] Sketch038
  FullyConstrained = true
  MapMode = 5
  Support = -> [XY_Plane018]
  sketch-geometry (2):
    g0: Circle CenterX=0 CenterY=0 CenterZ=0 NormalX=0 NormalY=0 NormalZ=1 AngleXU=0 Radius=26
    g1: Circle CenterX=0 CenterY=0 CenterZ=0 NormalX=0 NormalY=0 NormalZ=1 AngleXU=0 Radius=28
  constraints (4):
    c: Coincident(g0,g-1)
    c: Coincident(g1,g0)
    c: Diameter(g0) = 52
    c: Diameter(g1) = 56
FEATURE [Sketcher::SketchObject] Sketch039
  FullyConstrained = true
  MapMode = 5
  Support = -> [XY_Plane018]
  expr: Constraints[17] = <<var>>.humerusW
  expr: Constraints[16] = <<var>>.humerusW / 2
  sketch-geometry (9):
    g0: ArcOfCircle CenterX=0 CenterY=0 CenterZ=0 NormalX=0 NormalY=0 NormalZ=1 AngleXU=0 Radius=28 StartAngle=3.14159 EndAngle=6.28319
    g1: LineSegment StartX=-28 StartY=3.4e-15 StartZ=0 EndX=-28 EndY=-38.6375 EndZ=0
    g2: LineSegment StartX=-28 StartY=-38.6375 StartZ=0 EndX=28 EndY=-38.6375 EndZ=0
    g3: LineSegment StartX=28 StartY=-38.6375 StartZ=0 EndX=28 EndY=-7.1e-15 EndZ=0
    g4: Circle CenterX=-18 CenterY=-28.3187 CenterZ=0 NormalX=0 NormalY=0 NormalZ=1 AngleXU=0 Radius=2.25
    g5: Circle CenterX=18 CenterY=-28.3187 CenterZ=0 NormalX=0 NormalY=0 NormalZ=1 AngleXU=0 Radius=2.25
    g6: LineSegment StartX=-28 StartY=-18 StartZ=0 EndX=28 EndY=-18 EndZ=0
    g7: Circle CenterX=-18 CenterY=-28.3187 CenterZ=0 NormalX=0 NormalY=0 NormalZ=1 AngleXU=0 Radius=3.5
    g8: Circle CenterX=18 CenterY=-28.3187 CenterZ=0 NormalX=0 NormalY=0 NormalZ=1 AngleXU=0 Radius=3.5
  constraints (25):
    c: Coincident(g0,g-1)
    c: PointOnObject(g0,g-1)
    c: PointOnObject(g0,g-1)
    c: Coincident(g0,g1)
    c: Coincident(g1,g2)
    c: Horizontal(g2)
    c: Coincident(g2,g3)
    c: Coincident(g3,g0)
    c: Vertical(g3)
    c: Diameter(g0) = 56
    c: Vertical(g1)
    c: PointOnObject(g6,g1)
    c: PointOnObject(g6,g3)
    c: Horizontal(g6)
    c: Symmetric(g4,g5,g-2)
    c: DistanceX(g4,g5) = 36
    c: DistanceY(g4,g6) = 10.3187
    c: DistanceY(g1,g6) = 20.6375
    c: Diameter(g4) = 4.5
    c: Equal(g4,g5)
    c: DistanceY(g6,g0) = 18
    c: Coincident(g7,g4)
    c: Coincident(g8,g5)
    c: Diameter(g8) = 7
    c: Equal(g8,g7)
FEATURE [Sketcher::SketchObject] Sketch040
  FullyConstrained = true
  MapMode = 5
  Support = -> [XY_Plane018]
  sketch-geometry (2):
    g0: Circle CenterX=0 CenterY=0 CenterZ=0 NormalX=0 NormalY=0 NormalZ=1 AngleXU=0 Radius=9.55
    g1: Circle CenterX=0 CenterY=0 CenterZ=0 NormalX=0 NormalY=0 NormalZ=1 AngleXU=0 Radius=28
  constraints (4):
    c: Coincident(g0,g-1)
    c: Diameter(g0) = 19.1
    c: Coincident(g1,g0)
    c: Diameter(g1) = 56
FEATURE [PartDesign::Pad] Pad025
  AllowMultiFace = false
  Direction = (1,1,1)
  Length = 6
  Length2 = 100
  Profile = -> Sketch040
  Type = 0
FEATURE [PartDesign::Pad] Pad023
  AllowMultiFace = false
  BaseFeature = -> Pad025
  Direction = (1,1,1)
  Length = 15
  Length2 = 5
  Profile = -> Sketch038
  Type = 0
FEATURE [PartDesign::Pad] Pad024
  AllowMultiFace = false
  BaseFeature = -> Pad023
  Direction = (1,1,1)
  Length = 6
  Length2 = 5
  Profile = -> Sketch039
  Type = 0
FEATURE [Sketcher::SketchObject] Sketch041
  FullyConstrained = true
  MapMode = 5
  Placement = pos=(0,0,0) rot=(0.57735,0.57735,0.57735;2.0944rad)
  Support = -> [YZ_Plane018]
  sketch-geometry (3):
    g0: LineSegment StartX=9.55 StartY=0.866025 StartZ=0 EndX=10.05 EndY=0 EndZ=0
    g1: LineSegment StartX=9.55 StartY=0 StartZ=0 EndX=9.55 EndY=0.866025 EndZ=0
    g2: LineSegment StartX=9.55 StartY=0 StartZ=0 EndX=10.05 EndY=0 EndZ=0
  constraints (9):
    c: PointOnObject(g0,g-1)
    c: PointOnObject(g1,g-1)
    c: Vertical(g1)
    c: Coincident(g0,g1)
    c: Angle(g1,g0) = 0.523599
    c: Coincident(g2,g1)
    c: Coincident(g2,g0)
    c: DistanceX(g2,g2) = 0.5
    c: DistanceX(g-1,g1) = 9.55
FEATURE [PartDesign::Groove] Groove
  Angle = 360
  Axis = (-2e-16,3e-16,1)
  Base = (0,0,0)
  BaseFeature = -> Pad024
  Profile = -> Sketch041
  ReferenceAxis = -> Sketch041 [V_Axis]
FEATURE [Sketcher::SketchObject] Sketch065
  FullyConstrained = true
  MapMode = 5
  Placement = pos=(0,0,0) rot=(1,0,0;1.5708rad)
  Support = -> [XZ_Plane019]
  sketch-geometry (4):
    g0: LineSegment StartX=9.55 StartY=6 StartZ=0 EndX=7.55 EndY=8 EndZ=0
    g1: LineSegment StartX=7.55 StartY=8 StartZ=0 EndX=12.55 EndY=8 EndZ=0
    g2: LineSegment StartX=12.55 StartY=8 StartZ=0 EndX=12.55 EndY=6 EndZ=0
    g3: LineSegment StartX=12.55 StartY=6 StartZ=0 EndX=9.55 EndY=6 EndZ=0
  constraints (12):
    c: Coincident(g0,g1)
    c: Horizontal(g1)
    c: Coincident(g1,g2)
    c: Vertical(g2)
    c: Coincident(g2,g3)
    c: Coincident(g3,g0)
    c: Horizontal(g3)
    c: DistanceX(g-1,g0) = 9.55
    c: DistanceY(g2,g2) = 2
    c: DistanceY(g-1,g2) = 6
    c: Angle(g0,g1) = 0.785398
    c: DistanceX(g3,g3) = 3
FEATURE [PartDesign::Revolution] Revolution
  Angle = 360
  Axis = (0,-2e-16,1)
  Base = (0,0,0)
  BaseFeature = -> Groove
  Profile = -> Sketch065
  ReferenceAxis = -> Sketch065 [V_Axis]
  Reversed = true
FEATURE [Sketcher::SketchObject] Sketch091
  FullyConstrained = true
  MapMode = 5
  Support = -> [XY_Plane018]
  sketch-geometry (2):
    g0: Circle CenterX=0 CenterY=0 CenterZ=0 NormalX=0 NormalY=0 NormalZ=1 AngleXU=0 Radius=28
    g1: Circle CenterX=0 CenterY=0 CenterZ=0 NormalX=0 NormalY=0 NormalZ=1 AngleXU=0 Radius=24
  constraints (4):
    c: Coincident(g0,g-1)
    c: Coincident(g1,g0)
    c: Diameter(g0) = 56
    c: Diameter(g1) = 48
FEATURE [PartDesign::Pad] Pad056
  BaseFeature = -> Revolution
  Direction = (1,1,1)
  Length = 10
  Length2 = 100
  Profile = -> Sketch091
  Type = 0
FEATURE [Sketcher::SketchObject] Sketch098
  FullyConstrained = true
  MapMode = 5
  Support = -> [XY_Plane018]
  sketch-geometry (7):
    g0: LineSegment StartX=-26 StartY=8 StartZ=0 EndX=-44 EndY=8 EndZ=0
    g1: LineSegment StartX=-44 StartY=8 StartZ=0 EndX=-44 EndY=-4.5 EndZ=0
    g2: LineSegment StartX=-44 StartY=-4.5 StartZ=0 EndX=-26 EndY=-4.5 EndZ=0
    g3: LineSegment StartX=-26 StartY=-4.5 StartZ=0 EndX=-26 EndY=8 EndZ=0
    g4: Circle CenterX=-39 CenterY=0 CenterZ=0 NormalX=0 NormalY=0 NormalZ=1 AngleXU=0 Radius=2.55
    g5: Circle CenterX=-31 CenterY=0 CenterZ=0 NormalX=0 NormalY=0 NormalZ=1 AngleXU=0 Radius=2.55
    g6: Circle CenterX=0 CenterY=0 CenterZ=0 NormalX=0 NormalY=0 NormalZ=1 AngleXU=0 Radius=26
  constraints (20):
    c: Horizontal(g0)
    c: Coincident(g0,g1)
    c: Coincident(g1,g2)
    c: Horizontal(g2)
    c: Coincident(g2,g3)
    c: Coincident(g3,g0)
    c: Vertical(g3)
    c: PointOnObject(g4,g-1)
    c: PointOnObject(g5,g-1)
    c: DistanceX(g4,g5) = 8
    c: Diameter(g4) = 5.1
    c: Equal(g4,g5)
    c: DistanceX(g0,g4) = 5
    c: Coincident(g6,g-1)
    c: Diameter(g6) = 52
    c: Tangent(g3,g6)
    c: DistanceX(g5,g-1) = 31
    c: DistanceY(g1,g-1) = 4.5
    c: DistanceY(g-1,g0) = 8
    c: Vertical(g1)
FEATURE [PartDesign::Pad] Pad060
  BaseFeature = -> Pad056
  Direction = (1,1,1)
  Length = 27.5
  Length2 = 100
  Profile = -> Sketch098
  Type = 0
  expr: Length = <<var>>.J2BaseEncoderH
FEATURE [PartDesign::Body] Body007
  Group = -> [Sketch040,Pad025,Sketch038,Pad023,Sketch039,Pad024,Sketch041,Groove,Sketch065,Revolution,Sketch091,Pad056,Sketch098,Pad060]
  Origin = -> Origin018
  Tip = -> Pad060
COMPONENT P4 — recipe-attached ("J2_MTR_BRACKET_2V0", modeled in this document).
Construction recipe (the document's own serialized feature program — sketch geometry with constraints, then the solid features built on it; lengths are millimeters unless a unit is written):

FEATURE [Sketcher::SketchObject] Sketch030
  FullyConstrained = true
  MapMode = 5
  Support = -> [XY_Plane015]
  expr: Constraints[31] = <<var>>.motorJ0HoleD
  expr: Constraints[26] = <<var>>.motorJ0LocD
  expr: Constraints[24] = <<var>>.motorJ0HolePD
  sketch-geometry (32):
    g0: LineSegment StartX=-30 StartY=-10 StartZ=0 EndX=-30 EndY=10 EndZ=0
    g1: LineSegment StartX=20 StartY=30 StartZ=0 EndX=20 EndY=-3.6e-15 EndZ=0
    g2: LineSegment StartX=10 StartY=-10 StartZ=0 EndX=-30 EndY=-10 EndZ=0
    g3: LineSegment StartX=-30 StartY=10 StartZ=0 EndX=70 EndY=10 EndZ=0
    g4: LineSegment StartX=70 StartY=10 StartZ=0 EndX=70 EndY=-10 EndZ=0
    g5: LineSegment StartX=70 StartY=-10 StartZ=0 EndX=-30 EndY=-10 EndZ=0
    g6: LineSegment StartX=-30 StartY=-10 StartZ=0 EndX=-30 EndY=10 EndZ=0
    g7: ArcOfCircle CenterX=0 CenterY=30 CenterZ=0 NormalX=0 NormalY=0 NormalZ=1 AngleXU=0 Radius=20 StartAngle=2e-16 EndAngle=2.01011
    g8: Circle CenterX=0 CenterY=30 CenterZ=0 NormalX=0 NormalY=0 NormalZ=1 AngleXU=0 Radius=14
    g9: LineSegment StartX=-9.89949 StartY=39.8995 StartZ=0 EndX=9.89949 EndY=39.8995 EndZ=0
    g10: LineSegment StartX=9.89949 StartY=39.8995 StartZ=0 EndX=9.89949 EndY=20.1005 EndZ=0
    g11: LineSegment StartX=9.89949 StartY=20.1005 StartZ=0 EndX=-9.89949 EndY=20.1005 EndZ=0
    g12: LineSegment StartX=-9.89949 StartY=20.1005 StartZ=0 EndX=-9.89949 EndY=39.8995 EndZ=0
    g13: Circle CenterX=0 CenterY=30 CenterZ=0 NormalX=0 NormalY=0 NormalZ=1 AngleXU=0 Radius=11.1
    g14: Circle CenterX=-9.89949 CenterY=39.8995 CenterZ=0 NormalX=0 NormalY=0 NormalZ=1 AngleXU=0 Radius=1.65
    g15: Circle CenterX=9.89949 CenterY=39.8995 CenterZ=0 NormalX=0 NormalY=0 NormalZ=1 AngleXU=0 Radius=1.65
    g16: Circle CenterX=9.89949 CenterY=20.1005 CenterZ=0 NormalX=0 NormalY=0 NormalZ=1 AngleXU=0 Radius=1.65
    g17: Circle CenterX=-9.89949 CenterY=20.1005 CenterZ=0 NormalX=0 NormalY=0 NormalZ=1 AngleXU=0 Radius=1.65
    g18: Circle CenterX=0 CenterY=30 CenterZ=0 NormalX=0 NormalY=0 NormalZ=1 AngleXU=0 Radius=18
    g19: GeomPoint X=0 Y=12 Z=0
    g20: ArcOfCircle CenterX=-25 CenterY=0 CenterZ=0 NormalX=0 NormalY=0 NormalZ=1 AngleXU=0 Radius=2.25 StartAngle=1.5708 EndAngle=4.71239
    g21: ArcOfCircle CenterX=-10 CenterY=0 CenterZ=0 NormalX=0 NormalY=0 NormalZ=1 AngleXU=0 Radius=2.25 StartAngle=4.71239 EndAngle=7.85398
    g22: LineSegment StartX=-25 StartY=-2.25 StartZ=0 EndX=-10 EndY=-2.25 EndZ=0
    g23: LineSegment StartX=-25 StartY=2.25 StartZ=0 EndX=-10 EndY=2.25 EndZ=0
    g24: ArcOfCircle CenterX=1.2e-15 CenterY=0 CenterZ=0 NormalX=0 NormalY=0 NormalZ=1 AngleXU=0 Radius=2.25 StartAngle=1.5708 EndAngle=4.71239
    g25: ArcOfCircle CenterX=15 CenterY=-1e-16 CenterZ=0 NormalX=0 NormalY=0 NormalZ=1 AngleXU=0 Radius=2.25 StartAngle=4.71239 EndAngle=7.85398
    g26: LineSegment StartX=8e-16 StartY=-2.25 StartZ=0 EndX=15 EndY=-2.25 EndZ=0
    g27: LineSegment StartX=9e-16 StartY=2.25 StartZ=0 EndX=15 EndY=2.25 EndZ=0
    g28: LineSegment StartX=-30 StartY=10 StartZ=0 EndX=-30 EndY=38 EndZ=0
    g29: LineSegment StartX=-30 StartY=38 StartZ=0 EndX=-8.50644 EndY=48.1008 EndZ=0
    g30: ArcOfCircle CenterX=10 CenterY=2e-16 CenterZ=0 NormalX=0 NormalY=0 NormalZ=1 AngleXU=0 Radius=10 StartAngle=4.71239 EndAngle=6.28319
    g31: GeomPoint X=20 Y=-10 Z=0
  constraints (78):
    c: Vertical(g1)
    c: Horizontal(g2)
    c: Coincident(g3,g4)
    c: Coincident(g4,g5)
    c: Coincident(g5,g6)
    c: Coincident(g6,g3)
    c: Horizontal(g3)
    c: Horizontal(g5)
    c: Vertical(g4)
    c: Symmetric(g3,g5,g-1)
    c: PointOnObject(g7,g-2)
    c: Coincident(g8,g7)
    c: Coincident(g9,g10)
    c: Coincident(g10,g11)
    c: Coincident(g11,g12)
    c: Coincident(g12,g9)
    c: Horizontal(g9)
    c: Horizontal(g11)
    c: Vertical(g10)
    c: Vertical(g12)
    c: PointOnObject(g9,g8)
    c: PointOnObject(g10,g8)
    c: Equal(g9,g10)
    c: PointOnObject(g9,g8)
    c: Diameter(g8) = 28
    c: Coincident(g13,g7)
    c: Diameter(g13) = 22.2
    c: Coincident(g14,g9)
    c: Coincident(g15,g9)
    c: Coincident(g16,g10)
    c: Coincident(g17,g11)
    c: Diameter(g17) = 3.3
    c: Equal(g17,g16)
    c: Equal(g17,g15)
    c: Equal(g17,g14)
    c: Coincident(g18,g7)
    c: Diameter(g18) = 36
    c: PointOnObject(g19,g18)
    c: PointOnObject(g19,g-2)
    c: Diameter(g7) = 40
    c: Tangent(g20,g23)
    c: Tangent(g20,g22)
    c: Tangent(g22,g21)
    c: Tangent(g23,g21)
    c: Horizontal(g22)
    c: Equal(g20,g21)
    c: PointOnObject(g20,g-1)
    c: Tangent(g24,g27)
    c: Tangent(g24,g26)
    c: Tangent(g26,g25)
    c: Tangent(g27,g25)
    c: Horizontal(g26)
    c: Equal(g24,g25)
    c: DistanceX(g23,g23) = 15
    c: Diameter(g21) = 4.5
    c: Equal(g24,g21)
    c: Equal(g27,g23)
    c: DistanceX(g21,g24) = 10
    c: DistanceX(g0,g20) = 5
    c: DistanceY(g4,g4) = 20
    c: DistanceX(g5,g5) = 100
    c: Coincident(g3,g0)
    c: Tangent(g7,g1) = 1.5708
    c: DistanceX(g25,g31) = 5
    c: PointOnObject(g24,g-1)
    c: Coincident(g2,g5)
    c: Coincident(g0,g2)
    c: Coincident(g28,g0)
    c: Vertical(g28)
    c: Coincident(g29,g28)
    c: Tangent(g7,g29) = 1.5708
    c: DistanceY(g-1,g28) = 38
    c: DistanceY(g-1,g7) = 30
    c: PointOnObject(g31,g2)
    c: PointOnObject(g31,g1)
    c: Tangent(g2,g30) = 1.5708
    c: Tangent(g1,g30) = 1.5708
    c: Diameter(g30) = 20
FEATURE [Sketcher::SketchObject] Sketch031
  AttachmentOffset = pos=(0,0,6) rot=(0,0,1;0rad)
  FullyConstrained = true
  MapMode = 5
  Placement = pos=(0,0,6) rot=(0,0,1;0rad)
  Support = -> [XY_Plane015]
  expr: Constraints[28] = <<var>>.humerusW
  expr: Constraints[34] = <<var>>.motorJ0HolePD
  sketch-geometry (15):
    g0: Circle CenterX=9.89949 CenterY=39.8995 CenterZ=0 NormalX=0 NormalY=0 NormalZ=1 AngleXU=0 Radius=3.5
    g1: Circle CenterX=-9.89949 CenterY=39.8995 CenterZ=0 NormalX=0 NormalY=0 NormalZ=1 AngleXU=0 Radius=3.5
    g2: Circle CenterX=0 CenterY=30 CenterZ=0 NormalX=0 NormalY=0 NormalZ=1 AngleXU=0 Radius=14
    g3: LineSegment StartX=-9.89949 StartY=20.1005 StartZ=0 EndX=9.89949 EndY=20.1005 EndZ=0
    g4: LineSegment StartX=9.89949 StartY=20.1005 StartZ=0 EndX=9.89949 EndY=39.8995 EndZ=0
    g5: LineSegment StartX=9.89949 StartY=39.8995 StartZ=0 EndX=-9.89949 EndY=39.8995 EndZ=0
    g6: LineSegment StartX=-9.89949 StartY=39.8995 StartZ=0 EndX=-9.89949 EndY=20.1005 EndZ=0
    g7: Circle CenterX=-9.89949 CenterY=20.1005 CenterZ=0 NormalX=0 NormalY=0 NormalZ=1 AngleXU=0 Radius=3.5
    g8: Circle CenterX=9.89949 CenterY=20.1005 CenterZ=0 NormalX=0 NormalY=0 NormalZ=1 AngleXU=0 Radius=3.5
    g9: LineSegment StartX=-50 StartY=10.3187 StartZ=0 EndX=50 EndY=10.3187 EndZ=0
    g10: LineSegment StartX=50 StartY=10.3187 StartZ=0 EndX=50 EndY=-10.3187 EndZ=0
    g11: LineSegment StartX=50 StartY=-10.3187 StartZ=0 EndX=-50 EndY=-10.3187 EndZ=0
    g12: LineSegment StartX=-50 StartY=-10.3187 StartZ=0 EndX=-50 EndY=10.3187 EndZ=0
    g13: Circle CenterX=0 CenterY=30 CenterZ=0 NormalX=0 NormalY=0 NormalZ=1 AngleXU=0 Radius=18
    g14: GeomPoint X=0 Y=12 Z=0
  constraints (37):
    c: PointOnObject(g2,g-2)
    c: PointOnObject(g0,g2)
    c: Coincident(g3,g4)
    c: Coincident(g4,g5)
    c: Coincident(g5,g6)
    c: Coincident(g6,g3)
    c: Horizontal(g3)
    c: Horizontal(g5)
    c: Vertical(g4)
    c: Vertical(g6)
    c: PointOnObject(g3,g2)
    c: Coincident(g4,g0)
    c: Equal(g5,g6)
    c: Coincident(g5,g1)
    c: PointOnObject(g1,g2)
    c: Coincident(g7,g3)
    c: Coincident(g8,g3)
    c: Diameter(g8) = 7
    c: Equal(g8,g7)
    c: Equal(g8,g0)
    c: Equal(g8,g1)
    c: Coincident(g9,g10)
    c: Coincident(g10,g11)
    c: Coincident(g11,g12)
    c: Coincident(g12,g9)
    c: Horizontal(g11)
    c: Vertical(g12)
    c: Symmetric(g9,g10,g-1)
    c: DistanceY(g10,g10) = 20.6375
    c: DistanceX(g11,g11) = 100
    c: Coincident(g13,g2)
    c: Diameter(g13) = 36
    c: PointOnObject(g14,g13)
    c: PointOnObject(g14,g-2)
    c: Diameter(g2) = 28
    c: Symmetric(g9,g9,g-2)
    c: DistanceY(g-1,g2) = 30
FEATURE [Sketcher::SketchObject] Sketch032
  AttachmentOffset = pos=(0,0,-30) rot=(0,0,1;0rad)
  FullyConstrained = true
  MapMode = 5
  Placement = pos=(-30,6.7e-15,-6.7e-15) rot=(0.57735,0.57735,0.57735;2.0944rad)
  Support = -> [YZ_Plane015]
  expr: Constraints[2] = 6 - <<var>>.tensionerJ2ScrewH
  sketch-geometry (3):
    g0: Circle CenterX=0 CenterY=-3 CenterZ=0 NormalX=0 NormalY=0 NormalZ=1 AngleXU=0 Radius=5
    g1: Circle CenterX=0 CenterY=-3 CenterZ=0 NormalX=0 NormalY=0 NormalZ=1 AngleXU=0 Radius=3.5
    g2: Circle CenterX=30 CenterY=-3 CenterZ=0 NormalX=0 NormalY=0 NormalZ=1 AngleXU=0 Radius=5
  constraints (8):
    c: PointOnObject(g0,g-2)
    c: Diameter(g0) = 10
    c: DistanceY(g-1,g0) = -3
    c: Coincident(g1,g0)
    c: Diameter(g1) = 7
    c: Equal(g2,g0)
    c: Horizontal(g2,g0)
    c: DistanceX(g-1,g2) = 30
FEATURE [PartDesign::Pad] Pad018
  Direction = (1,1,1)
  Length = 6
  Length2 = 100
  Profile = -> Sketch030
  Refine = true
  Type = 0
FEATURE [Sketcher::SketchObject] Sketch036
  FullyConstrained = true
  MapMode = 5
  Support = -> [XY_Plane015]
  sketch-geometry (17):
    g0: LineSegment StartX=20 StartY=10 StartZ=0 EndX=20 EndY=-3.42695e-11 EndZ=0
    g1: LineSegment StartX=-30 StartY=-10 StartZ=0 EndX=-30 EndY=10 EndZ=0
    g2: ArcOfCircle CenterX=-25 CenterY=0 CenterZ=0 NormalX=0 NormalY=0 NormalZ=1 AngleXU=0 Radius=2.25 StartAngle=1.5708 EndAngle=4.71239
    g3: ArcOfCircle CenterX=-10 CenterY=2e-16 CenterZ=0 NormalX=0 NormalY=0 NormalZ=1 AngleXU=0 Radius=2.25 StartAngle=4.71239 EndAngle=7.85398
    g4: LineSegment StartX=-25 StartY=-2.25 StartZ=0 EndX=-10 EndY=-2.25 EndZ=0
    g5: LineSegment StartX=-25 StartY=2.25 StartZ=0 EndX=-10 EndY=2.25 EndZ=0
    g6: ArcOfCircle CenterX=2.6e-15 CenterY=0 CenterZ=0 NormalX=0 NormalY=0 NormalZ=1 AngleXU=0 Radius=2.25 StartAngle=1.5708 EndAngle=4.71239
    g7: ArcOfCircle CenterX=15 CenterY=2e-16 CenterZ=0 NormalX=0 NormalY=0 NormalZ=1 AngleXU=0 Radius=2.25 StartAngle=4.71239 EndAngle=7.85398
    g8: LineSegment StartX=2.6e-15 StartY=-2.25 StartZ=0 EndX=15 EndY=-2.25 EndZ=0
    g9: LineSegment StartX=2.4e-15 StartY=2.25 StartZ=0 EndX=15 EndY=2.25 EndZ=0
    g10: LineSegment StartX=-20 StartY=10 StartZ=0 EndX=20 EndY=10 EndZ=0
    g11: LineSegment StartX=10 StartY=-10 StartZ=0 EndX=-30 EndY=-10 EndZ=0
    g12: LineSegment StartX=-20 StartY=10 StartZ=0 EndX=-20 EndY=38 EndZ=0
    g13: LineSegment StartX=-20 StartY=38 StartZ=0 EndX=-30 EndY=38 EndZ=0
    g14: LineSegment StartX=-30 StartY=38 StartZ=0 EndX=-30 EndY=10 EndZ=0
    g15: ArcOfCircle CenterX=10 CenterY=3.28e-13 CenterZ=0 NormalX=0 NormalY=0 NormalZ=1 AngleXU=0 Radius=10 StartAngle=4.71239 EndAngle=6.28319
    g16: GeomPoint X=20 Y=-10 Z=0
  constraints (44):
    c: Vertical(g0)
    c: DistanceX(g1,g16) = 50
    c: DistanceX(g-1,g16) = 20
    c: Tangent(g2,g5)
    c: Tangent(g2,g4)
    c: Tangent(g4,g3)
    c: Tangent(g5,g3)
    c: Horizontal(g4)
    c: Equal(g2,g3)
    c: PointOnObject(g2,g-1)
    c: Tangent(g6,g9)
    c: Tangent(g6,g8)
    c: Tangent(g8,g7)
    c: Tangent(g9,g7)
    c: Horizontal(g8)
    c: Equal(g6,g7)
    c: PointOnObject(g6,g-1)
    c: Equal(g6,g3)
    c: Equal(g5,g9)
    c: DistanceX(g9,g9) = 15
    c: DistanceX(g3,g6) = 10
    c: DistanceX(g7,g0) = 5
    c: Diameter(g2) = 4.5
    c: Coincident(g10,g0)
    c: Coincident(g11,g1)
    c: DistanceY(g16,g0) = 20
    c: Horizontal(g11)
    c: Horizontal(g10)
    c: Symmetric(g1,g1,g-1)
    c: Coincident(g12,g13)
    c: Coincident(g13,g14)
    c: Vertical(g14)
    c: Coincident(g14,g1)
    c: Vertical(g12)
    c: DistanceX(g13,g12) = 10
    c: Horizontal(g13)
    c: DistanceY(g-1,g13) = 38
    c: Coincident(g10,g12)
    c: Horizontal(g10,g1)
    c: PointOnObject(g16,g11)
    c: PointOnObject(g16,g0)
    c: Tangent(g11,g15) = 1.5708
    c: Tangent(g0,g15) = 1.5708
    c: Diameter(g15) = 20
FEATURE [PartDesign::Pad] Pad021
  BaseFeature = -> Pad018
  Direction = (1,1,1)
  Length = 10
  Length2 = 100
  Profile = -> Sketch036
  Reversed = true
  Type = 0
FEATURE [PartDesign::Pocket] Pocket013
  BaseFeature = -> Pad021
  Length = 2
  Length2 = 100
  Profile = -> Sketch032
  Reversed = true
  Type = 0
FEATURE [PartDesign::Hole] Hole004
  BaseFeature = -> Pocket013
  Depth = 25
  DepthType = 1
  Diameter = 3.4
  DrillForDepth = false
  DrillPoint = 1
  DrillPointAngle = 118
  HoleCutCountersinkAngle = 90
  HoleCutCustomValues = false
  HoleCutDepth = 0
  HoleCutDiameter = 6.1
  HoleCutType = 2
  ModelActualThread = false
  Profile = -> Sketch031
  Tapered = false
  TaperedAngle = 90
  ThreadAngle = 0
  ThreadClass = 0
  ThreadCutOffInner = 0
  ThreadCutOffOuter = 0
  ThreadDirection = 0
  ThreadFit = 0
  ThreadPitch = 0
  ThreadSize = 9
  ThreadType = 1
  Threaded = false
FEATURE [PartDesign::Body] Body006
  Group = -> [Sketch030,Pad018,Sketch031,Sketch032,Sketch036,Pad021,Pocket013,Hole004]
  Origin = -> Origin015
  Tip = -> Hole004
COMPONENT P5 — recipe-attached ("SHAFT_J2_1V0", modeled in this document).
Construction recipe (the document's own serialized feature program — sketch geometry with constraints, then the solid features built on it; lengths are millimeters unless a unit is written):

FEATURE [Sketcher::SketchObject] Sketch042
  FullyConstrained = false
  MapMode = 5
  Support = -> [XY_Plane020]
  sketch-geometry (3):
    g0: Circle CenterX=0 CenterY=0 CenterZ=0 NormalX=0 NormalY=0 NormalZ=1 AngleXU=0 Radius=3
    g1: LineSegment StartX=-1.65831 StartY=2.5 StartZ=0 EndX=1.65831 EndY=2.5 EndZ=0
    g2: ArcOfCircle CenterX=0 CenterY=0 CenterZ=0 NormalX=0 NormalY=0 NormalZ=1 AngleXU=0 Radius=3 StartAngle=2.15648 EndAngle=7.2683
  constraints (8):
    c: Coincident(g0,g-1)
    c: Diameter(g0) = 6
    c: PointOnObject(g1,g0)
    c: Horizontal(g1)
    c: Coincident(g2,g-1)
    c: Coincident(g2,g1)
    c: Coincident(g2,g1)
    c: DistanceY(g-1,g1) = 2.5
FEATURE [PartDesign::Pad] Pad026
  Direction = (1,1,1)
  Length = 35
  Length2 = 100
  Profile = -> Sketch042
  Refine = true
  Type = 0
FEATURE [PartDesign::CoordinateSystem] LCS_1
  AttacherType = Attacher::AttachEngine3D
  MapMode = 5
  Placement = pos=(0,0,0) rot=(1,0,0;3.14159rad)
  Support = -> [Pad026]
FEATURE [PartDesign::CoordinateSystem] LCS_2
  AttacherType = Attacher::AttachEngine3D
  MapMode = 5
  Placement = pos=(0,0,35) rot=(0,0,1;0rad)
  Support = -> [Pad026]
FEATURE [PartDesign::Body] Body008  label="SHAFT_J2_1V0"
  Group = -> [Sketch042,Pad026,LCS_1,LCS_2]
  Origin = -> Origin020
  Tip = -> Pad026
COMPONENT P6 — recipe-attached ("ENCODER_BRACKET_1V0", modeled in this document).
Construction recipe (the document's own serialized feature program — sketch geometry with constraints, then the solid features built on it; lengths are millimeters unless a unit is written):

FEATURE [Sketcher::SketchObject] Sketch072
  FullyConstrained = true
  MapMode = 5
  Support = -> [XY_Plane034]
  sketch-geometry (14):
    g0: LineSegment StartX=-7 StartY=-51 StartZ=0 EndX=5 EndY=-51 EndZ=0
    g1: LineSegment StartX=5 StartY=-51 StartZ=0 EndX=5 EndY=-21 EndZ=0
    g2: LineSegment StartX=5 StartY=-5 StartZ=0 EndX=-7 EndY=-5 EndZ=0
    g3: LineSegment StartX=-7 StartY=-5 StartZ=0 EndX=-7 EndY=-51 EndZ=0
    g4: LineSegment StartX=-3 StartY=4 StartZ=0 EndX=3 EndY=4 EndZ=0
    g5: LineSegment StartX=3 StartY=4 StartZ=0 EndX=3 EndY=-21 EndZ=0
    g6: LineSegment StartX=3 StartY=-21 StartZ=0 EndX=-3 EndY=-21 EndZ=0
    g7: LineSegment StartX=-3 StartY=-21 StartZ=0 EndX=-3 EndY=4 EndZ=0
    g8: Circle CenterX=0 CenterY=-10 CenterZ=0 NormalX=0 NormalY=0 NormalZ=1 AngleXU=0 Radius=1.32
    g9: LineSegment StartX=-3 StartY=-13.5 StartZ=0 EndX=5 EndY=-13.5 EndZ=0
    g10: LineSegment StartX=5 StartY=-21 StartZ=0 EndX=-3 EndY=-21 EndZ=0
    g11: LineSegment StartX=-3 StartY=-21 StartZ=0 EndX=-3 EndY=-13.5 EndZ=0
    g12: Circle CenterX=0 CenterY=0 CenterZ=0 NormalX=0 NormalY=0 NormalZ=1 AngleXU=0 Radius=33
    g13: LineSegment StartX=5 StartY=-13.5 StartZ=0 EndX=5 EndY=-5 EndZ=0
  constraints (39):
    c: Coincident(g0,g1)
    c: Coincident(g13,g2)
    c: Coincident(g2,g3)
    c: Coincident(g3,g0)
    c: Horizontal(g0)
    c: Vertical(g1)
    c: Vertical(g3)
    c: DistanceY(g0,g-1) = 51
    c: Coincident(g4,g5)
    c: Coincident(g5,g6)
    c: Coincident(g6,g7)
    c: Coincident(g7,g4)
    c: Horizontal(g6)
    c: Vertical(g5)
    c: Vertical(g7)
    c: DistanceY(g5,g5) = 25
    c: Symmetric(g4,g4,g-2)
    c: DistanceX(g4,g4) = 6
    c: PointOnObject(g8,g-2)
    c: Diameter(g8) = 2.64
    c: DistanceY(g8,g4) = 14
    c: Coincident(g10,g11)
    c: Coincident(g11,g9)
    c: Horizontal(g10)
    c: Vertical(g11)
    c: DistanceY(g10,g9) = 7.5
    c: Coincident(g12,g-1)
    c: Diameter(g12) = 66
    c: Horizontal(g2)
    c: DistanceX(g-1,g13) = 5
    c: DistanceY(g8,g13) = 5
    c: DistanceY(g-1,g4) = 4
    c: DistanceX(g2,g9) = 4
    c: DistanceX(g10,g-1) = 3
    c: Coincident(g1,g10)
    c: Coincident(g13,g9)
    c: Tangent(g1,g13)
    c: Horizontal(g9)
    c: Horizontal(g1,g5)
FEATURE [Sketcher::SketchObject] Sketch073
  FullyConstrained = true
  MapMode = 5
  Support = -> [XY_Plane034]
  sketch-geometry (6):
    g0: LineSegment StartX=-6 StartY=4 StartZ=0 EndX=6 EndY=4 EndZ=0
    g1: LineSegment StartX=6 StartY=4 StartZ=0 EndX=6 EndY=-21 EndZ=0
    g2: LineSegment StartX=6 StartY=-21 StartZ=0 EndX=-3 EndY=-21 EndZ=0
    g3: LineSegment StartX=-3 StartY=-21 StartZ=0 EndX=-3 EndY=-8 EndZ=0
    g4: ArcOfCircle CenterX=-6 CenterY=-8 CenterZ=0 NormalX=0 NormalY=0 NormalZ=1 AngleXU=0 Radius=3 StartAngle=0 EndAngle=1.5708
    g5: LineSegment StartX=-6 StartY=-5 StartZ=0 EndX=-6 EndY=4 EndZ=0
  constraints (19):
    c: Coincident(g0,g1)
    c: Coincident(g1,g2)
    c: Coincident(g2,g3)
    c: Horizontal(g0)
    c: Horizontal(g2)
    c: Vertical(g1)
    c: Vertical(g3)
    c: DistanceY(g-1,g0) = 4
    c: DistanceX(g-1,g0) = 6
    c: DistanceY(g3,g0) = 25
    c: Coincident(g3,g4)
    c: Vertical(g4,g4)
    c: Horizontal(g4,g3)
    c: Diameter(g4) = 6
    c: DistanceX(g3,g-1) = 3
    c: Coincident(g5,g4)
    c: Coincident(g5,g0)
    c: Vertical(g5)
    c: DistanceY(g5,g5) = 9
FEATURE [PartDesign::CoordinateSystem] LCS_0014
  AttacherType = Attacher::AttachEngine3D
  MapMode = 2
  Support = -> [X_Axis034]
FEATURE [PartDesign::Pad] Pad047
  Direction = (1,1,1)
  Length = 9
  Length2 = 100
  Profile = -> Sketch072
  Type = 0
FEATURE [PartDesign::Pocket] Pocket023
  BaseFeature = -> Pad047
  Length = 1.6
  Length2 = 100
  Profile = -> Sketch073
  Reversed = true
  Type = 0
FEATURE [Sketcher::SketchObject] Sketch074
  AttachmentOffset = pos=(0,0,9) rot=(0,0,1;0rad)
  FullyConstrained = true
  MapMode = 5
  Placement = pos=(0,0,9) rot=(0,0,1;0rad)
  Support = -> [XY_Plane034]
  sketch-geometry (2):
    g0: Circle CenterX=0 CenterY=-38 CenterZ=0 NormalX=0 NormalY=0 NormalZ=1 AngleXU=0 Radius=1.5
    g1: Circle CenterX=0 CenterY=-46 CenterZ=0 NormalX=0 NormalY=0 NormalZ=1 AngleXU=0 Radius=1.5
  constraints (6):
    c: PointOnObject(g0,g-2)
    c: PointOnObject(g1,g-2)
    c: Diameter(g1) = 3
    c: Equal(g1,g0)
    c: DistanceY(g1,g0) = 8
    c: DistanceY(g0,g-1) = 38
FEATURE [PartDesign::Hole] Hole001
  BaseFeature = -> Pocket023
  Depth = 25
  DepthType = 1
  Diameter = 3.3
  DrillForDepth = false
  DrillPoint = 1
  DrillPointAngle = 118
  HoleCutCountersinkAngle = 82
  HoleCutCustomValues = false
  HoleCutDepth = 0
  HoleCutDiameter = 6
  HoleCutType = 2
  ModelActualThread = false
  Profile = -> Sketch074
  Tapered = false
  TaperedAngle = 90
  ThreadAngle = 0
  ThreadClass = 0
  ThreadCutOffInner = 0
  ThreadCutOffOuter = 0
  ThreadDirection = 0
  ThreadFit = 0
  ThreadPitch = 0
  ThreadSize = 3
  ThreadType = 3
  Threaded = false
FEATURE [PartDesign::Body] Body_3
  Group = -> [LCS_0014,Sketch072,Sketch073,Pad047,Pocket023,Sketch074,Hole001]
  Origin = -> Origin034
  Tip = -> Hole001
COMPONENT P7 — recipe-attached ("ENCODER_BRACKET_A_1V0", modeled in this document).
Construction recipe (the document's own serialized feature program — sketch geometry with constraints, then the solid features built on it; lengths are millimeters unless a unit is written):

FEATURE [Sketcher::SketchObject] Sketch099
  FullyConstrained = true
  MapMode = 5
  Support = -> [XY_Plane040]
  sketch-geometry (14):
    g0: LineSegment StartX=-7 StartY=-44 StartZ=0 EndX=5 EndY=-44 EndZ=0
    g1: LineSegment StartX=5 StartY=-44 StartZ=0 EndX=5 EndY=-21 EndZ=0
    g2: LineSegment StartX=-3 StartY=4 StartZ=0 EndX=3 EndY=4 EndZ=0
    g3: LineSegment StartX=3 StartY=4 StartZ=0 EndX=3 EndY=-21 EndZ=0
    g4: LineSegment StartX=3 StartY=-21 StartZ=0 EndX=-3 EndY=-21 EndZ=0
    g5: LineSegment StartX=-3 StartY=-21 StartZ=0 EndX=-3 EndY=4 EndZ=0
    g6: Circle CenterX=0 CenterY=-10 CenterZ=0 NormalX=0 NormalY=0 NormalZ=1 AngleXU=0 Radius=1.32
    g7: LineSegment StartX=-3 StartY=-13.5 StartZ=0 EndX=5 EndY=-13.5 EndZ=0
    g8: LineSegment StartX=5 StartY=-21 StartZ=0 EndX=-3 EndY=-21 EndZ=0
    g9: LineSegment StartX=-3 StartY=-21 StartZ=0 EndX=-3 EndY=-13.5 EndZ=0
    g10: Circle CenterX=0 CenterY=0 CenterZ=0 NormalX=0 NormalY=0 NormalZ=1 AngleXU=0 Radius=26
    g11: LineSegment StartX=5 StartY=-13.5 StartZ=0 EndX=5 EndY=-5 EndZ=0
    g12: LineSegment StartX=-7 StartY=-5 StartZ=0 EndX=-7 EndY=-44 EndZ=0
    g13: LineSegment StartX=-7 StartY=-5 StartZ=0 EndX=5 EndY=-5 EndZ=0
  constraints (38):
    c: Coincident(g0,g1)
    c: Horizontal(g0)
    c: Vertical(g1)
    c: DistanceY(g0,g-1) = 44
    c: Coincident(g2,g3)
    c: Coincident(g3,g4)
    c: Coincident(g4,g5)
    c: Coincident(g5,g2)
    c: Horizontal(g4)
    c: Vertical(g3)
    c: Vertical(g5)
    c: DistanceY(g3,g3) = 25
    c: Symmetric(g2,g2,g-2)
    c: DistanceX(g2,g2) = 6
    c: PointOnObject(g6,g-2)
    c: Diameter(g6) = 2.64
    c: DistanceY(g6,g2) = 14
    c: Coincident(g8,g9)
    c: Coincident(g9,g7)
    c: Horizontal(g8)
    c: Vertical(g9)
    c: DistanceY(g8,g7) = 7.5
    c: Coincident(g10,g-1)
    c: Diameter(g10) = 52
    c: Horizontal(g7)
    c: Coincident(g1,g8)
    c: Coincident(g11,g7)
    c: Tangent(g1,g11)
    c: Vertical(g12)
    c: Coincident(g0,g12)
    c: DistanceX(g12,g-1) = 7
    c: DistanceY(g-1,g2) = 4
    c: DistanceX(g-1,g0) = 5
    c: Coincident(g8,g4)
    c: Coincident(g13,g12)
    c: Coincident(g13,g11)
    c: Horizontal(g13)
    c: DistanceY(g6,g11) = 5
FEATURE [Sketcher::SketchObject] Sketch100
  FullyConstrained = true
  MapMode = 5
  Support = -> [XY_Plane040]
  sketch-geometry (6):
    g0: LineSegment StartX=6 StartY=-21 StartZ=0 EndX=-3 EndY=-21 EndZ=0
    g1: LineSegment StartX=6 StartY=4 StartZ=0 EndX=6 EndY=-21 EndZ=0
    g2: LineSegment StartX=-6 StartY=4 StartZ=0 EndX=6 EndY=4 EndZ=0
    g3: LineSegment StartX=-3 StartY=-21 StartZ=0 EndX=-3 EndY=-8 EndZ=0
    g4: ArcOfCircle CenterX=-6 CenterY=-8 CenterZ=0 NormalX=0 NormalY=0 NormalZ=1 AngleXU=0 Radius=3 StartAngle=0 EndAngle=1.5708
    g5: LineSegment StartX=-6 StartY=-5 StartZ=0 EndX=-6 EndY=4 EndZ=0
  constraints (19):
    c: Horizontal(g0)
    c: DistanceY(g0,g2) = 25
    c: Coincident(g1,g0)
    c: Vertical(g1)
    c: DistanceY(g-1,g1) = 4
    c: Coincident(g2,g1)
    c: Horizontal(g2)
    c: DistanceX(g-1,g1) = 6
    c: DistanceX(g0,g-1) = 3
    c: Coincident(g3,g0)
    c: Vertical(g3)
    c: Coincident(g4,g3)
    c: Coincident(g5,g4)
    c: Coincident(g5,g2)
    c: Vertical(g5)
    c: Diameter(g4) = 6
    c: Vertical(g4,g4)
    c: Horizontal(g4,g3)
    c: DistanceY(g5,g5) = 9
FEATURE [PartDesign::Pad] Pad061
  Direction = (1,1,1)
  Length = 8
  Length2 = 100
  Profile = -> Sketch099
  Type = 0
FEATURE [PartDesign::Pocket] Pocket030
  BaseFeature = -> Pad061
  Length = 1.6
  Length2 = 100
  Profile = -> Sketch100
  Reversed = true
  Type = 0
FEATURE [PartDesign::CoordinateSystem] LCS_0018
  AttacherType = Attacher::AttachEngine3D
  MapMode = 2
  Support = -> [X_Axis040]
FEATURE [Sketcher::SketchObject] Sketch101
  AttachmentOffset = pos=(0,0,8) rot=(0,0,1;0rad)
  FullyConstrained = true
  MapMode = 5
  Placement = pos=(0,0,8) rot=(0,0,1;0rad)
  Support = -> [XY_Plane040]
  sketch-geometry (2):
    g0: Circle CenterX=0 CenterY=-31 CenterZ=0 NormalX=0 NormalY=0 NormalZ=1 AngleXU=0 Radius=1.5
    g1: Circle CenterX=0 CenterY=-39 CenterZ=0 NormalX=0 NormalY=0 NormalZ=1 AngleXU=0 Radius=1.5
  constraints (6):
    c: PointOnObject(g0,g-2)
    c: PointOnObject(g1,g-2)
    c: Diameter(g1) = 3
    c: Equal(g1,g0)
    c: DistanceY(g1,g0) = 8
    c: DistanceY(g0,g-1) = 31
FEATURE [PartDesign::Hole] Hole006
  BaseFeature = -> Pocket030
  Depth = 25
  DepthType = 1
  Diameter = 3.3
  DrillForDepth = false
  DrillPoint = 1
  DrillPointAngle = 118
  HoleCutCountersinkAngle = 82
  HoleCutCustomValues = false
  HoleCutDepth = 0
  HoleCutDiameter = 6
  HoleCutType = 2
  ModelActualThread = false
  Profile = -> Sketch101
  Tapered = false
  TaperedAngle = 90
  ThreadAngle = 0
  ThreadClass = 0
  ThreadCutOffInner = 0
  ThreadCutOffOuter = 0
  ThreadDirection = 0
  ThreadFit = 0
  ThreadPitch = 0
  ThreadSize = 3
  ThreadType = 3
  Threaded = false
FEATURE [PartDesign::Body] Body_004
  Group = -> [LCS_0018,Sketch099,Sketch100,Pad061,Pocket030,Sketch101,Hole006]
  Origin = -> Origin040
  Tip = -> Hole006
COMPONENT P8 — recipe-attached ("ENCODER_PCB_1V0", modeled in this document).
Construction recipe (the document's own serialized feature program — sketch geometry with constraints, then the solid features built on it; lengths are millimeters unless a unit is written):

FEATURE [PartDesign::CoordinateSystem] LCS_0023
  AttacherType = Attacher::AttachEngine3D
  MapMode = 2
  Support = -> [X_Axis045]
FEATURE [Sketcher::SketchObject] Sketch107
  FullyConstrained = true
  MapMode = 5
  Support = -> [XY_Plane045]
  sketch-geometry (5):
    g0: LineSegment StartX=-3 StartY=-21 StartZ=0 EndX=3 EndY=-21 EndZ=0
    g1: LineSegment StartX=3 StartY=-21 StartZ=0 EndX=3 EndY=4 EndZ=0
    g2: LineSegment StartX=3 StartY=4 StartZ=0 EndX=-3 EndY=4 EndZ=0
    g3: LineSegment StartX=-3 StartY=4 StartZ=0 EndX=-3 EndY=-21 EndZ=0
    g4: Circle CenterX=0 CenterY=-10 CenterZ=0 NormalX=0 NormalY=0 NormalZ=1 AngleXU=0 Radius=1.75
  constraints (14):
    c: Coincident(g0,g1)
    c: Coincident(g1,g2)
    c: Coincident(g2,g3)
    c: Coincident(g3,g0)
    c: Horizontal(g0)
    c: Vertical(g1)
    c: Vertical(g3)
    c: Symmetric(g1,g2,g-2)
    c: DistanceY(g3,g3) = 25
    c: DistanceY(g-1,g2) = 4
    c: DistanceX(g2,g2) = 6
    c: PointOnObject(g4,g-2)
    c: Diameter(g4) = 3.5
    c: DistanceY(g4,g1) = 14
FEATURE [PartDesign::Pad] Pad065
  Direction = (1,1,1)
  Length = 1.6
  Length2 = 100
  Profile = -> Sketch107
  Type = 0
FEATURE [PartDesign::Body] Body_5
  Group = -> [LCS_0023,Sketch107,Pad065]
  Origin = -> Origin045
  Tip = -> Pad065
COMPONENT P9 — recipe-attached ("HUMERUS_2V0", modeled in this document).
Construction recipe (the document's own serialized feature program — sketch geometry with constraints, then the solid features built on it; lengths are millimeters unless a unit is written):

FEATURE [Sketcher::SketchObject] Sketch086
  FullyConstrained = true
  MapMode = 5
  Support = -> [XY_Plane013]
  expr: Constraints[39] = <<var>>.humerusW
  sketch-geometry (16):
    g0: LineSegment StartX=5.15937 StartY=-10.3187 StartZ=0 EndX=5.15937 EndY=10.3187 EndZ=0
    g1: LineSegment StartX=5.15937 StartY=10.3187 StartZ=0 EndX=-5.15937 EndY=10.3187 EndZ=0
    g2: LineSegment StartX=-5.15937 StartY=10.3187 StartZ=0 EndX=-5.15937 EndY=5.55625 EndZ=0
    g3: LineSegment StartX=-5.15937 StartY=5.55625 StartZ=0 EndX=-2.15937 EndY=5.55625 EndZ=0
    g4: LineSegment StartX=-2.15937 StartY=5.55625 StartZ=0 EndX=-2.15937 EndY=6.55625 EndZ=0
    g5: LineSegment StartX=-2.15937 StartY=6.55625 StartZ=0 EndX=-4.15937 EndY=6.55625 EndZ=0
    g6: LineSegment StartX=-4.15937 StartY=6.55625 StartZ=0 EndX=-4.15937 EndY=9.31875 EndZ=0
    g7: LineSegment StartX=-4.15937 StartY=9.31875 StartZ=0 EndX=3.63537 EndY=9.31875 EndZ=0
    g8: LineSegment StartX=3.63537 StartY=9.31875 StartZ=0 EndX=3.63537 EndY=-9.31875 EndZ=0
    g9: LineSegment StartX=3.63537 StartY=-9.31875 StartZ=0 EndX=-4.15937 EndY=-9.31875 EndZ=0
    g10: LineSegment StartX=-4.15937 StartY=-9.31875 StartZ=0 EndX=-4.15937 EndY=-6.55625 EndZ=0
    g11: LineSegment StartX=-4.15937 StartY=-6.55625 StartZ=0 EndX=-2.15937 EndY=-6.55625 EndZ=0
    g12: LineSegment StartX=-2.15937 StartY=-6.55625 StartZ=0 EndX=-2.15937 EndY=-5.55625 EndZ=0
    g13: LineSegment StartX=-2.15937 StartY=-5.55625 StartZ=0 EndX=-5.15937 EndY=-5.55625 EndZ=0
    g14: LineSegment StartX=-5.15937 StartY=-5.55625 StartZ=0 EndX=-5.15937 EndY=-10.3187 EndZ=0
    g15: LineSegment StartX=-5.15937 StartY=-10.3187 StartZ=0 EndX=5.15937 EndY=-10.3187 EndZ=0
  constraints (45):
    c: Coincident(g0,g1)
    c: Coincident(g1,g2)
    c: Vertical(g2)
    c: Coincident(g2,g3)
    c: Coincident(g3,g4)
    c: Coincident(g4,g5)
    c: Horizontal(g5)
    c: Coincident(g5,g6)
    c: Coincident(g6,g7)
    c: Horizontal(g7)
    c: Coincident(g7,g8)
    c: Vertical(g8)
    c: Coincident(g8,g9)
    c: Horizontal(g9)
    c: Coincident(g9,g10)
    c: Vertical(g10)
    c: Coincident(g10,g11)
    c: Horizontal(g11)
    c: Coincident(g11,g12)
    c: Vertical(g12)
    c: Coincident(g12,g13)
    c: Horizontal(g13)
    c: Coincident(g13,g14)
    c: Vertical(g14)
    c: Coincident(g14,g15)
    c: Coincident(g15,g0)
    c: DistanceX(g7,g0) = 1.524
    c: DistanceY(g6,g1) = 1
    c: Vertical(g6)
    c: Horizontal(g3)
    c: Vertical(g4)
    c: DistanceY(g4,g4) = 1
    c: DistanceX(g2,g5) = 1
    c: Symmetric(g2,g13,g-1)
    c: Equal(g3,g13)
    c: Equal(g12,g4)
    c: Equal(g2,g14)
    c: Equal(g10,g6)
    c: Equal(g11,g5)
    c: DistanceY(g0,g0) = 20.6375
    c: DistanceX(g15,g15) = 10.3187
    c: DistanceY(g13,g2) = 11.1125
    c: Symmetric(g1,g0,g-2)
    c: Symmetric(g0,g0,g-1)
    c: DistanceX(g3,g3) = 3
FEATURE [PartDesign::Pad] Pad053
  Direction = (1,1,1)
  Length = 304.8
  Length2 = 100
  Profile = -> Sketch086
  Refine = true
  Type = 0
FEATURE [Sketcher::SketchObject] Sketch087
  FullyConstrained = true
  MapMode = 5
  Placement = pos=(0,0,0) rot=(0.57735,0.57735,0.57735;2.0944rad)
  Support = -> [YZ_Plane013]
  sketch-geometry (8):
    g0: Circle CenterX=0 CenterY=10 CenterZ=0 NormalX=0 NormalY=0 NormalZ=1 AngleXU=0 Radius=2.35
    g1: Circle CenterX=0 CenterY=45 CenterZ=0 NormalX=0 NormalY=0 NormalZ=1 AngleXU=0 Radius=2.35
    g2: Circle CenterX=0 CenterY=80 CenterZ=0 NormalX=0 NormalY=0 NormalZ=1 AngleXU=0 Radius=2.1
    g3: Circle CenterX=0 CenterY=105 CenterZ=0 NormalX=0 NormalY=0 NormalZ=1 AngleXU=0 Radius=2.1
    g4: Circle CenterX=0 CenterY=133 CenterZ=0 NormalX=0 NormalY=0 NormalZ=1 AngleXU=0 Radius=2.1
    g5: Circle CenterX=0 CenterY=153 CenterZ=0 NormalX=0 NormalY=0 NormalZ=1 AngleXU=0 Radius=2.1
    g6: Circle CenterX=0 CenterY=294.8 CenterZ=0 NormalX=0 NormalY=0 NormalZ=1 AngleXU=0 Radius=2.1
    g7: Circle CenterX=0 CenterY=258.8 CenterZ=0 NormalX=0 NormalY=0 NormalZ=1 AngleXU=0 Radius=2.1
  constraints (24):
    c: PointOnObject(g0,g-2)
    c: PointOnObject(g1,g-2)
    c: Diameter(g1) = 4.7
    c: Equal(g1,g0)
    c: DistanceY(g0,g1) = 35
    c: DistanceY(g-1,g0) = 10
    c: PointOnObject(g2,g-2)
    c: PointOnObject(g3,g-2)
    c: Equal(g2,g3)
    c: DistanceY(g1,g2) = 35
    c: DistanceY(g2,g3) = 25
    c: PointOnObject(g4,g-2)
    c: PointOnObject(g5,g-2)
    c: Equal(g4,g5)
    c: Equal(g5,g3)
    c: DistanceY(g4,g5) = 20
    c: DistanceY(g3,g4) = 28
    c: PointOnObject(g6,g-2)
    c: PointOnObject(g7,g-2)
    c: DistanceY(g7,g6) = 36
    c: Equal(g6,g7)
    c: Equal(g7,g5)
    c: DistanceY(g-1,g6) = 294.8
    c: Diameter(g2) = 4.2
FEATURE [PartDesign::Pocket] Pocket027
  BaseFeature = -> Pad053
  Length = 5
  Length2 = 100
  Profile = -> Sketch087
  Refine = true
  Reversed = true
  Type = 1
FEATURE [PartDesign::Body] Body005
  Group = -> [Sketch086,Pad053,Sketch087,Pocket027]
  Origin = -> Origin013
  Tip = -> Pocket027
COMPONENT P10 — recipe-attached ("J3_BASE_2V0", modeled in this document).
Construction recipe (the document's own serialized feature program — sketch geometry with constraints, then the solid features built on it; lengths are millimeters unless a unit is written):

FEATURE [Sketcher::SketchObject] Sketch051
  FullyConstrained = true
  MapMode = 5
  Support = -> [XY_Plane025]
  expr: Constraints[17] = <<var>>.humerusW / 2
  expr: Constraints[14] = <<var>>.humerusW
  sketch-geometry (36):
    g0: ArcOfCircle CenterX=0 CenterY=0 CenterZ=0 NormalX=0 NormalY=0 NormalZ=1 AngleXU=0 Radius=9.5 StartAngle=1.75606 EndAngle=2.95632
    g1: LineSegment StartX=-29 StartY=-39.6375 StartZ=0 EndX=13 EndY=-39.6375 EndZ=0
    g2: LineSegment StartX=18 StartY=-34.6375 StartZ=0 EndX=18 EndY=-19 EndZ=0
    g3: Circle CenterX=8 CenterY=-29.3188 CenterZ=0 NormalX=0 NormalY=0 NormalZ=1 AngleXU=0 Radius=1.7
    g4: LineSegment StartX=-34 StartY=-19 StartZ=0 EndX=66 EndY=-19 EndZ=0
    g5: LineSegment StartX=66 StartY=-19 StartZ=0 EndX=66 EndY=-39.6375 EndZ=0
    g6: LineSegment StartX=66 StartY=-39.6375 StartZ=0 EndX=-34 EndY=-39.6375 EndZ=0
    g7: LineSegment StartX=-34 StartY=-39.6375 StartZ=0 EndX=-34 EndY=-19 EndZ=0
    g8: LineSegment StartX=-34 StartY=-34.6375 StartZ=0 EndX=-34 EndY=5 EndZ=0
    g9: Circle CenterX=-24 CenterY=-29.3188 CenterZ=0 NormalX=0 NormalY=0 NormalZ=1 AngleXU=0 Radius=1.7
    g10: Circle CenterX=0 CenterY=0 CenterZ=0 NormalX=0 NormalY=0 NormalZ=1 AngleXU=0 Radius=11
    g11: LineSegment StartX=-11 StartY=1.8e-15 StartZ=0 EndX=0 EndY=11 EndZ=0
    g12: LineSegment StartX=0 StartY=11 StartZ=0 EndX=11 EndY=-1.8e-15 EndZ=0
    g13: LineSegment StartX=11 StartY=-1.1e-15 StartZ=0 EndX=0 EndY=-11 EndZ=0
    g14: LineSegment StartX=0 StartY=-11 StartZ=0 EndX=-11 EndY=1.8e-15 EndZ=0
    g15: ArcOfCircle CenterX=-11 CenterY=1.8e-15 CenterZ=0 NormalX=0 NormalY=0 NormalZ=1 AngleXU=0 Radius=1.75 StartAngle=1.5708 EndAngle=4.71239
    g16: ArcOfCircle CenterX=11 CenterY=-1.1e-15 CenterZ=0 NormalX=0 NormalY=0 NormalZ=1 AngleXU=0 Radius=1.75 StartAngle=4.71239 EndAngle=7.85398
    g17: LineSegment StartX=-11 StartY=-1.75 StartZ=0 EndX=-9.33742 EndY=-1.75 EndZ=0
    g18: LineSegment StartX=-11 StartY=1.75 StartZ=0 EndX=-9.33742 EndY=1.75 EndZ=0
    g19: ArcOfCircle CenterX=0 CenterY=-11 CenterZ=0 NormalX=0 NormalY=0 NormalZ=1 AngleXU=0 Radius=1.75 StartAngle=3.14159 EndAngle=6.28319
    g20: ArcOfCircle CenterX=0 CenterY=11 CenterZ=0 NormalX=0 NormalY=0 NormalZ=1 AngleXU=0 Radius=1.75 StartAngle=-9e-16 EndAngle=3.14159
    g21: LineSegment StartX=1.75 StartY=-11 StartZ=0 EndX=1.75 EndY=-9.33742 EndZ=0
    g22: LineSegment StartX=-1.75 StartY=-11 StartZ=0 EndX=-1.75 EndY=-9.33742 EndZ=0
    g23: LineSegment StartX=9.33742 StartY=1.75 StartZ=0 EndX=11 EndY=1.75 EndZ=0
    g24: LineSegment StartX=-1.75 StartY=9.33742 StartZ=0 EndX=-1.75 EndY=11 EndZ=0
    g25: LineSegment StartX=1.75 StartY=9.33742 StartZ=0 EndX=1.75 EndY=11 EndZ=0
    g26: LineSegment StartX=9.33742 StartY=-1.75 StartZ=0 EndX=11 EndY=-1.75 EndZ=0
    g27: ArcOfCircle CenterX=0 CenterY=0 CenterZ=0 NormalX=0 NormalY=0 NormalZ=1 AngleXU=0 Radius=9.5 StartAngle=3.32686 EndAngle=4.52712
    g28: ArcOfCircle CenterX=0 CenterY=0 CenterZ=0 NormalX=0 NormalY=0 NormalZ=1 AngleXU=0 Radius=9.5 StartAngle=4.89766 EndAngle=6.09792
    g29: ArcOfCircle CenterX=0 CenterY=0 CenterZ=0 NormalX=0 NormalY=0 NormalZ=1 AngleXU=0 Radius=9.5 StartAngle=0.185269 EndAngle=1.38553
    g30: ArcOfCircle CenterX=0 CenterY=0 CenterZ=0 NormalX=0 NormalY=0 NormalZ=1 AngleXU=0 Radius=18 StartAngle=0 EndAngle=1.97606
    g31: LineSegment StartX=-7.09677 StartY=16.5419 StartZ=0 EndX=-34 EndY=5 EndZ=0
    g32: LineSegment StartX=18 StartY=0 StartZ=0 EndX=18 EndY=-19 EndZ=0
    g33: ArcOfCircle CenterX=-29 CenterY=-34.6375 CenterZ=0 NormalX=0 NormalY=0 NormalZ=1 AngleXU=0 Radius=5 StartAngle=3.14159 EndAngle=4.71239
    g34: ArcOfCircle CenterX=13 CenterY=-34.6375 CenterZ=0 NormalX=0 NormalY=0 NormalZ=1 AngleXU=0 Radius=5 StartAngle=4.71239 EndAngle=6.28319
    g35: Circle CenterX=0 CenterY=0 CenterZ=0 NormalX=0 NormalY=0 NormalZ=1 AngleXU=0 Radius=17.272
  constraints (91):
    c: Coincident(g0,g-1)
    c: Diameter(g0) = 19
    c: Horizontal(g1)
    c: Vertical(g2)
    c: Diameter(g3) = 3.4
    c: Coincident(g4,g5)
    c: Coincident(g5,g6)
    c: Coincident(g6,g7)
    c: Coincident(g7,g4)
    c: Horizontal(g4)
    c: Horizontal(g6)
    c: Vertical(g5)
    c: Vertical(g7)
    c: DistanceY(g4,g-1) = 19
    c: DistanceY(g5,g5) = 20.6375
    c: PointOnObject(g2,g4)
    c: DistanceX(g6,g6) = 100
    c: DistanceY(g3,g2) = 10.3187
    c: Equal(g9,g3)
    c: DistanceX(g9,g3) = 32
    c: DistanceX(g6,g9) = 10
    c: Horizontal(g9,g3)
    c: Coincident(g10,g0)
    c: Coincident(g11,g12)
    c: Coincident(g12,g13)
    c: Coincident(g13,g14)
    c: Coincident(g14,g11)
    c: Diameter(g10) = 22
    c: Tangent(g15,g18)
    c: Tangent(g15,g17)
    c: Equal(g15,g16)
    c: Coincident(g15,g11)
    c: Coincident(g16,g12)
    c: PointOnObject(g16,g10)
    c: PointOnObject(g15,g10)
    c: PointOnObject(g11,g10)
    c: Equal(g12,g11)
    c: Diameter(g15) = 3.5
    c: Tangent(g19,g22)
    c: Tangent(g19,g21)
    c: Equal(g19,g20)
    c: Coincident(g19,g13)
    c: Coincident(g20,g11)
    c: Equal(g20,g15)
    c: Tangent(g18,g23)
    c: Tangent(g22,g24)
    c: Tangent(g21,g25)
    c: Tangent(g17,g26)
    c: Equal(g0,g27)
    c: Coincident(g0,g27)
    c: Equal(g27,g28)
    c: Coincident(g27,g28)
    c: Equal(g28,g29)
    c: Coincident(g28,g29)
    c: Tangent(g25,g20) = -1.5708
    c: Tangent(g24,g20) = 1.5708
    c: Tangent(g23,g16) = 1.5708
    c: Tangent(g26,g16) = -1.5708
    c: Coincident(g30,g0)
    c: PointOnObject(g30,g-1)
    c: Diameter(g30) = 36
    c: Tangent(g31,g30) = -1.5708
    c: Coincident(g32,g30)
    c: Coincident(g32,g2)
    c: Vertical(g32)
    c: Coincident(g22,g27)
    c: Coincident(g28,g21)
    c: Coincident(g26,g28)
    c: Coincident(g23,g29)
    c: Coincident(g25,g29)
    c: Coincident(g24,g0)
    c: Coincident(g18,g0)
    c: Coincident(g17,g27)
    c: Tangent(g8,g33) = 1.5708
    c: Tangent(g1,g33) = -1.5708
    c: Tangent(g2,g34) = -1.5708
    c: Tangent(g1,g34) = -1.5708
    c: Equal(g34,g33)
    c: Vertical(g8)
    c: PointOnObject(g1,g6)
    c: Diameter(g33) = 10
    c: DistanceX(g3,g2) = 10
    c: Coincident(g35,g0)
    c: Diameter(g35) = 34.544
    c: DistanceX(g8,g9) = 10
    c: Coincident(g8,g31)
    c: DistanceY(g-1,g8) = 5
    c: Perpendicular(g14,g11)
    c: Perpendicular(g12,g13)
    c: Perpendicular(g12,g11)
    c: PointOnObject(g20,g-2)
FEATURE [PartDesign::Pad] Pad032
  Direction = (1,1,1)
  Length = 5
  Length2 = 100
  Profile = -> Sketch051
  Type = 0
FEATURE [Sketcher::SketchObject] Sketch103
  AttachmentOffset = pos=(0,0,5) rot=(0,0,1;0rad)
  FullyConstrained = true
  MapMode = 5
  Placement = pos=(0,0,5) rot=(0,0,1;0rad)
  Support = -> [XY_Plane025]
  sketch-geometry (7):
    g0: LineSegment StartX=-26 StartY=5 StartZ=0 EndX=-44 EndY=5 EndZ=0
    g1: LineSegment StartX=-44 StartY=5 StartZ=0 EndX=-44 EndY=-7 EndZ=0
    g2: LineSegment StartX=-44 StartY=-7 StartZ=0 EndX=-26 EndY=-7 EndZ=0
    g3: LineSegment StartX=-26 StartY=-7 StartZ=0 EndX=-26 EndY=5 EndZ=0
    g4: Circle CenterX=-39 CenterY=0 CenterZ=0 NormalX=0 NormalY=0 NormalZ=1 AngleXU=0 Radius=1.092
    g5: Circle CenterX=-31 CenterY=0 CenterZ=0 NormalX=0 NormalY=0 NormalZ=1 AngleXU=0 Radius=1.092
    g6: Circle CenterX=0 CenterY=0 CenterZ=0 NormalX=0 NormalY=0 NormalZ=1 AngleXU=0 Radius=26
  constraints (20):
    c: Horizontal(g0)
    c: Coincident(g0,g1)
    c: Coincident(g1,g2)
    c: Horizontal(g2)
    c: Coincident(g2,g3)
    c: Coincident(g3,g0)
    c: Vertical(g3)
    c: PointOnObject(g4,g-1)
    c: PointOnObject(g5,g-1)
    c: DistanceX(g4,g5) = 8
    c: Diameter(g4) = 2.184
    c: Equal(g4,g5)
    c: DistanceX(g0,g4) = 5
    c: Coincident(g6,g-1)
    c: Diameter(g6) = 52
    c: Tangent(g3,g6)
    c: DistanceX(g5,g-1) = 31
    c: DistanceY(g1,g-1) = 7
    c: DistanceY(g-1,g0) = 5
    c: Vertical(g1)
FEATURE [PartDesign::Pad] Pad062
  BaseFeature = -> Pad032
  Direction = (1,1,1)
  Length = 23.5
  Length2 = 100
  Profile = -> Sketch103
  Refine = true
  Reversed = true
  Type = 0
  expr: Length = <<var>>.J3BaseEncoderH
FEATURE [PartDesign::Body] Body012
  Group = -> [Sketch051,Pad032,Sketch103,Pad062]
  Origin = -> Origin025
  Tip = -> Pad062
COMPONENT P11 — recipe-attached ("J3_PLATE_2V0", modeled in this document).
Construction recipe (the document's own serialized feature program — sketch geometry with constraints, then the solid features built on it; lengths are millimeters unless a unit is written):

FEATURE [PartDesign::CoordinateSystem] LCS_0021
  AttacherType = Attacher::AttachEngine3D
  MapMode = 2
  Support = -> [X_Axis043]
FEATURE [Sketcher::SketchObject] Sketch104
  FullyConstrained = true
  MapMode = 5
  Support = -> [XY_Plane043]
  sketch-geometry (7):
    g0: ArcOfCircle CenterX=0 CenterY=0 CenterZ=0 NormalX=0 NormalY=0 NormalZ=1 AngleXU=0 Radius=20 StartAngle=3.14159 EndAngle=6.28319
    g1: LineSegment StartX=-20 StartY=2.4e-15 StartZ=0 EndX=-20 EndY=20 EndZ=0
    g2: LineSegment StartX=-20 StartY=20 StartZ=0 EndX=20 EndY=20 EndZ=0
    g3: LineSegment StartX=20 StartY=20 StartZ=0 EndX=20 EndY=-3.91e-14 EndZ=0
    g4: Circle CenterX=0 CenterY=0 CenterZ=0 NormalX=0 NormalY=0 NormalZ=1 AngleXU=0 Radius=3.05
    g5: Circle CenterX=-15 CenterY=15 CenterZ=0 NormalX=0 NormalY=0 NormalZ=1 AngleXU=0 Radius=1.7272
    g6: Circle CenterX=15 CenterY=15 CenterZ=0 NormalX=0 NormalY=0 NormalZ=1 AngleXU=0 Radius=1.7272
  constraints (19):
    c: Coincident(g0,g-1)
    c: PointOnObject(g0,g-1)
    c: PointOnObject(g0,g-1)
    c: Tangent(g0,g1) = 1.5708
    c: Coincident(g1,g2)
    c: Horizontal(g2)
    c: Coincident(g2,g3)
    c: Coincident(g3,g0)
    c: Vertical(g3)
    c: Coincident(g4,g0)
    c: Diameter(g4) = 6.1
    c: Diameter(g0) = 40
    c: DistanceY(g1,g1) = 20
    c: Symmetric(g6,g5,g-2)
    c: Diameter(g5) = 3.4544
    c: Equal(g5,g6)
    c: DistanceY(g6,g2) = 5
    c: DistanceX(g6,g2) = 5
    c: DistanceX(g5,g6) = 30
FEATURE [Sketcher::SketchObject] Sketch105
  AttachmentOffset = pos=(0,0,5) rot=(0,0,1;0rad)
  FullyConstrained = true
  MapMode = 5
  Placement = pos=(0,0,5) rot=(0,0,1;0rad)
  Support = -> [XY_Plane043]
  sketch-geometry (8):
    g0: LineSegment StartX=-8 StartY=8 StartZ=0 EndX=8 EndY=8 EndZ=0
    g1: LineSegment StartX=8 StartY=8 StartZ=0 EndX=8 EndY=-8 EndZ=0
    g2: LineSegment StartX=8 StartY=-8 StartZ=0 EndX=-8 EndY=-8 EndZ=0
    g3: LineSegment StartX=-8 StartY=-8 StartZ=0 EndX=-8 EndY=8 EndZ=0
    g4: Circle CenterX=-8 CenterY=8 CenterZ=0 NormalX=0 NormalY=0 NormalZ=1 AngleXU=0 Radius=1.75
    g5: Circle CenterX=8 CenterY=8 CenterZ=0 NormalX=0 NormalY=0 NormalZ=1 AngleXU=0 Radius=1.75
    g6: Circle CenterX=8 CenterY=-8 CenterZ=0 NormalX=0 NormalY=0 NormalZ=1 AngleXU=0 Radius=1.75
    g7: Circle CenterX=-8 CenterY=-8 CenterZ=0 NormalX=0 NormalY=0 NormalZ=1 AngleXU=0 Radius=1.75
  constraints (18):
    c: Coincident(g0,g1)
    c: Coincident(g1,g2)
    c: Coincident(g2,g3)
    c: Coincident(g3,g0)
    c: Horizontal(g2)
    c: Vertical(g1)
    c: Symmetric(g0,g0,g-2)
    c: Symmetric(g0,g2,g-1)
    c: Equal(g3,g0)
    c: Coincident(g4,g0)
    c: Coincident(g5,g0)
    c: Coincident(g6,g1)
    c: Coincident(g7,g2)
    c: Diameter(g4) = 3.5
    c: Equal(g4,g7)
    c: Equal(g4,g6)
    c: Equal(g4,g5)
    c: DistanceY(g1,g1) = 16
FEATURE [PartDesign::Pad] Pad063
  Direction = (1,1,1)
  Length = 5
  Length2 = 100
  Profile = -> Sketch104
  Refine = true
  Type = 0
FEATURE [PartDesign::Hole] Hole008
  BaseFeature = -> Pad063
  Depth = 25
  DepthType = 1
  Diameter = 4.3
  DrillForDepth = false
  DrillPoint = 1
  DrillPointAngle = 118
  HoleCutCountersinkAngle = 82
  HoleCutCustomValues = false
  HoleCutDepth = 0
  HoleCutDiameter = 8.298
  HoleCutType = 2
  ModelActualThread = false
  Profile = -> Sketch105
  Refine = true
  Tapered = false
  TaperedAngle = 90
  ThreadAngle = 0
  ThreadClass = 0
  ThreadCutOffInner = 0
  ThreadCutOffOuter = 0
  ThreadDirection = 0
  ThreadFit = 0
  ThreadPitch = 0
  ThreadSize = 5
  ThreadType = 3
  Threaded = false
FEATURE [Sketcher::SketchObject] Sketch106
  AttachmentOffset = pos=(0,0,1.5) rot=(0,0,1;0rad)
  FullyConstrained = true
  MapMode = 5
  Placement = pos=(0,0,1.5) rot=(0,0,1;0rad)
  Support = -> [XY_Plane043]
  sketch-geometry (1):
    g0: Circle CenterX=0 CenterY=0 CenterZ=0 NormalX=0 NormalY=0 NormalZ=1 AngleXU=0 Radius=3.5
  constraints (2):
    c: Coincident(g0,g-1)
    c: Diameter(g0) = 7
FEATURE [PartDesign::Pad] Pad064
  BaseFeature = -> Hole008
  Direction = (1,1,1)
  Length = 1
  Length2 = 100
  Profile = -> Sketch106
  Refine = true
  Type = 0
FEATURE [PartDesign::Body] Body_4
  Group = -> [LCS_0021,Sketch104,Sketch105,Pad063,Hole008,Sketch106,Pad064]
  Origin = -> Origin043
  Tip = -> Pad064
COMPONENT P12 — recipe-attached ("PCB_BRACKET_1V0", modeled in this document).
Construction recipe (the document's own serialized feature program — sketch geometry with constraints, then the solid features built on it; lengths are millimeters unless a unit is written):

FEATURE [PartDesign::CoordinateSystem] LCS_0025
  AttacherType = Attacher::AttachEngine3D
  MapMode = 2
  Support = -> [X_Axis047]
FEATURE [Sketcher::SketchObject] Sketch108
  FullyConstrained = true
  MapMode = 5
  Support = -> [XY_Plane047]
  sketch-geometry (20):
    g0: LineSegment StartX=-41.5 StartY=-35.5 StartZ=0 EndX=41.5 EndY=-35.5 EndZ=0
    g1: LineSegment StartX=41.5 StartY=-35.5 StartZ=0 EndX=41.5 EndY=35.5 EndZ=0
    g2: LineSegment StartX=41.5 StartY=35.5 StartZ=0 EndX=-41.5 EndY=35.5 EndZ=0
    g3: LineSegment StartX=-41.5 StartY=35.5 StartZ=0 EndX=-41.5 EndY=-35.5 EndZ=0
    g4: LineSegment StartX=-37.5 StartY=31.5 StartZ=0 EndX=37.5 EndY=31.5 EndZ=0
    g5: LineSegment StartX=37.5 StartY=31.5 StartZ=0 EndX=37.5 EndY=-31.5 EndZ=0
    g6: LineSegment StartX=37.5 StartY=-31.5 StartZ=0 EndX=-37.5 EndY=-31.5 EndZ=0
    g7: LineSegment StartX=-37.5 StartY=-31.5 StartZ=0 EndX=-37.5 EndY=31.5 EndZ=0
    g8: Circle CenterX=-37.5 CenterY=31.5 CenterZ=0 NormalX=0 NormalY=0 NormalZ=1 AngleXU=0 Radius=1.95
    g9: Circle CenterX=37.5 CenterY=31.5 CenterZ=0 NormalX=0 NormalY=0 NormalZ=1 AngleXU=0 Radius=1.95
    g10: Circle CenterX=37.5 CenterY=-31.5 CenterZ=0 NormalX=0 NormalY=0 NormalZ=1 AngleXU=0 Radius=1.95
    g11: Circle CenterX=-37.5 CenterY=-31.5 CenterZ=0 NormalX=0 NormalY=0 NormalZ=1 AngleXU=0 Radius=1.95
    g12: ArcOfCircle CenterX=-37.5 CenterY=31.5 CenterZ=0 NormalX=0 NormalY=0 NormalZ=1 AngleXU=0 Radius=4 StartAngle=4.71239 EndAngle=6.28319
    g13: ArcOfCircle CenterX=37.5 CenterY=31.5 CenterZ=0 NormalX=0 NormalY=0 NormalZ=1 AngleXU=0 Radius=4 StartAngle=3.14159 EndAngle=4.71239
    g14: ArcOfCircle CenterX=37.5 CenterY=-31.5 CenterZ=0 NormalX=0 NormalY=0 NormalZ=1 AngleXU=0 Radius=4 StartAngle=1.5708 EndAngle=3.14159
    g15: ArcOfCircle CenterX=-37.5 CenterY=-31.5 CenterZ=0 NormalX=0 NormalY=0 NormalZ=1 AngleXU=0 Radius=4 StartAngle=0 EndAngle=1.5708
    g16: LineSegment StartX=-37.5 StartY=-27.5 StartZ=0 EndX=-37.5 EndY=27.5 EndZ=0
    g17: LineSegment StartX=-33.5 StartY=31.5 StartZ=0 EndX=33.5 EndY=31.5 EndZ=0
    g18: LineSegment StartX=37.5 StartY=27.5 StartZ=0 EndX=37.5 EndY=-27.5 EndZ=0
    g19: LineSegment StartX=33.5 StartY=-31.5 StartZ=0 EndX=-33.5 EndY=-31.5 EndZ=0
  constraints (52):
    c: Coincident(g0,g1)
    c: Coincident(g1,g2)
    c: Coincident(g2,g3)
    c: Coincident(g3,g0)
    c: Horizontal(g0)
    c: Vertical(g1)
    c: Symmetric(g2,g1,g-2)
    c: Symmetric(g2,g0,g-1)
    c: Coincident(g4,g5)
    c: Coincident(g5,g6)
    c: Coincident(g6,g7)
    c: Coincident(g7,g4)
    c: Horizontal(g6)
    c: Vertical(g5)
    c: DistanceY(g7,g7) = 63
    c: Symmetric(g4,g6,g-1)
    c: DistanceX(g4,g4) = 75
    c: Symmetric(g4,g4,g-2)
    c: Coincident(g8,g4)
    c: Coincident(g9,g4)
    c: Coincident(g10,g5)
    c: Coincident(g11,g6)
    c: Diameter(g11) = 3.9
    c: Equal(g11,g10)
    c: Equal(g11,g9)
    c: Equal(g11,g8)
    c: DistanceY(g8,g2) = 4
    c: DistanceX(g2,g8) = 4
    c: Coincident(g12,g8)
    c: PointOnObject(g12,g7)
    c: PointOnObject(g12,g4)
    c: Coincident(g13,g9)
    c: PointOnObject(g13,g4)
    c: PointOnObject(g13,g5)
    c: Coincident(g14,g10)
    c: PointOnObject(g14,g5)
    c: PointOnObject(g14,g6)
    c: Coincident(g15,g11)
    c: PointOnObject(g15,g6)
    c: PointOnObject(g15,g7)
    c: Coincident(g16,g15)
    c: Coincident(g16,g12)
    c: Coincident(g17,g12)
    c: Coincident(g17,g13)
    c: Coincident(g18,g13)
    c: Coincident(g18,g14)
    c: Coincident(g19,g14)
    c: Coincident(g19,g15)
    c: Diameter(g12) = 8
    c: Equal(g12,g15)
    c: Equal(g12,g13)
    c: Equal(g12,g14)
FEATURE [PartDesign::Pad] Pad066
  Direction = (1,1,1)
  Length = 4
  Length2 = 100
  Profile = -> Sketch108
  Refine = true
  Type = 0
FEATURE [Sketcher::SketchObject] Sketch109
  FullyConstrained = true
  MapMode = 5
  Support = -> [XY_Plane047]
  sketch-geometry (14):
    g0: Circle CenterX=-25 CenterY=0 CenterZ=0 NormalX=0 NormalY=0 NormalZ=1 AngleXU=0 Radius=2.25
    g1: Circle CenterX=25 CenterY=0 CenterZ=0 NormalX=0 NormalY=0 NormalZ=1 AngleXU=0 Radius=2.25
    g2: LineSegment StartX=-5 StartY=-33 StartZ=0 EndX=-5 EndY=-5 EndZ=0
    g3: LineSegment StartX=-5 StartY=-5 StartZ=0 EndX=-40 EndY=-5 EndZ=0
    g4: LineSegment StartX=-40 StartY=-5 StartZ=0 EndX=-40 EndY=5 EndZ=0
    g5: LineSegment StartX=-40 StartY=5 StartZ=0 EndX=-5 EndY=5 EndZ=0
    g6: LineSegment StartX=-5 StartY=5 StartZ=0 EndX=-5 EndY=33 EndZ=0
    g7: LineSegment StartX=-5 StartY=33 StartZ=0 EndX=5 EndY=33 EndZ=0
    g8: LineSegment StartX=5 StartY=33 StartZ=0 EndX=5 EndY=5 EndZ=0
    g9: LineSegment StartX=5 StartY=5 StartZ=0 EndX=40 EndY=5 EndZ=0
    g10: LineSegment StartX=40 StartY=5 StartZ=0 EndX=40 EndY=-5 EndZ=0
    g11: LineSegment StartX=40 StartY=-5 StartZ=0 EndX=5 EndY=-5 EndZ=0
    g12: LineSegment StartX=5 StartY=-5 StartZ=0 EndX=5 EndY=-33 EndZ=0
    g13: LineSegment StartX=5 StartY=-33 StartZ=0 EndX=-5 EndY=-33 EndZ=0
  constraints (37):
    c: PointOnObject(g0,g-1)
    c: Diameter(g1) = 4.5
    c: Equal(g1,g0)
    c: Symmetric(g0,g1,g-2)
    c: DistanceX(g0,g1) = 50
    c: Vertical(g2)
    c: Coincident(g2,g3)
    c: Horizontal(g3)
    c: Coincident(g3,g4)
    c: Coincident(g4,g5)
    c: Horizontal(g5)
    c: Coincident(g5,g6)
    c: Coincident(g6,g7)
    c: Horizontal(g7)
    c: Coincident(g7,g8)
    c: Vertical(g8)
    c: Coincident(g8,g9)
    c: Horizontal(g9)
    c: Coincident(g9,g10)
    c: Vertical(g10)
    c: Coincident(g10,g11)
    c: Horizontal(g11)
    c: Coincident(g11,g12)
    c: Vertical(g12)
    c: Coincident(g12,g13)
    c: Coincident(g13,g2)
    c: Vertical(g6)
    c: Symmetric(g4,g3,g-1)
    c: DistanceY(g4,g4) = 10
    c: Equal(g7,g4)
    c: Equal(g4,g13)
    c: Equal(g13,g10)
    c: Symmetric(g2,g12,g-2)
    c: DistanceX(g4,g9) = 80
    c: DistanceY(g2,g6) = 66
    c: Symmetric(g2,g6,g-1)
    c: Symmetric(g4,g9,g-2)
FEATURE [PartDesign::Pad] Pad067
  BaseFeature = -> Pad066
  Direction = (1,1,1)
  Length = 4
  Length2 = 100
  Profile = -> Sketch109
  Refine = true
  Type = 0
FEATURE [PartDesign::Body] Body_6
  Group = -> [LCS_0025,Sketch108,Pad066,Sketch109,Pad067]
  Origin = -> Origin047
  Tip = -> Pad067
COMPONENT P13 — recipe-attached ("J0_PLATE_2V0", modeled in this document).
Construction recipe (the document's own serialized feature program — sketch geometry with constraints, then the solid features built on it; lengths are millimeters unless a unit is written):

FEATURE [Sketcher::SketchObject] Sketch008
  FullyConstrained = true
  MapMode = 5
  Support = -> [XY_Plane006]
  sketch-geometry (2):
    g0: Circle CenterX=0 CenterY=0 CenterZ=0 NormalX=0 NormalY=0 NormalZ=1 AngleXU=0 Radius=3.1
    g1: Circle CenterX=0 CenterY=0 CenterZ=0 NormalX=0 NormalY=0 NormalZ=1 AngleXU=0 Radius=27
  constraints (4):
    c: Diameter(g0) = 6.2
    c: Coincident(g0,g-1)
    c: Coincident(g1,g0)
    c: Diameter(g1) = 54
FEATURE [PartDesign::Pad] Pad007
  AllowMultiFace = false
  Direction = (1,1,1)
  Length = 8
  Length2 = 100
  Profile = -> Sketch008
  Type = 0
FEATURE [Sketcher::SketchObject] Sketch012
  AttachmentOffset = pos=(0,0,8) rot=(0,0,1;0rad)
  FullyConstrained = true
  MapMode = 5
  Placement = pos=(0,0,8) rot=(0,0,1;0rad)
  Support = -> [XY_Plane006]
  expr: Constraints[16] = <<var>>.hubHoleD
  expr: Constraints[15] = <<var>>.hubHolePD
  sketch-geometry (9):
    g0: LineSegment StartX=-6.9148 StartY=6.9148 StartZ=0 EndX=6.9148 EndY=6.9148 EndZ=0
    g1: LineSegment StartX=6.9148 StartY=6.9148 StartZ=0 EndX=6.9148 EndY=-6.9148 EndZ=0
    g2: LineSegment StartX=6.9148 StartY=-6.9148 StartZ=0 EndX=-6.9148 EndY=-6.9148 EndZ=0
    g3: LineSegment StartX=-6.9148 StartY=-6.9148 StartZ=0 EndX=-6.9148 EndY=6.9148 EndZ=0
    g4: Circle CenterX=-6.9148 CenterY=6.9148 CenterZ=0 NormalX=0 NormalY=0 NormalZ=1 AngleXU=0 Radius=1.905
    g5: Circle CenterX=6.9148 CenterY=6.9148 CenterZ=0 NormalX=0 NormalY=0 NormalZ=1 AngleXU=0 Radius=1.905
    g6: Circle CenterX=6.9148 CenterY=-6.9148 CenterZ=0 NormalX=0 NormalY=0 NormalZ=1 AngleXU=0 Radius=1.905
    g7: Circle CenterX=-6.9148 CenterY=-6.9148 CenterZ=0 NormalX=0 NormalY=0 NormalZ=1 AngleXU=0 Radius=1.905
    g8: LineSegment StartX=-6.9148 StartY=6.9148 StartZ=0 EndX=6.9148 EndY=-6.9148 EndZ=0
  constraints (20):
    c: Coincident(g0,g1)
    c: Coincident(g1,g2)
    c: Coincident(g2,g3)
    c: Coincident(g3,g0)
    c: Horizontal(g2)
    c: Vertical(g1)
    c: Symmetric(g0,g0,g-2)
    c: Symmetric(g0,g2,g-1)
    c: Equal(g3,g0)
    c: Coincident(g4,g0)
    c: Coincident(g5,g0)
    c: Coincident(g6,g1)
    c: Coincident(g7,g2)
    c: Coincident(g8,g4)
    c: Coincident(g8,g6)
    c: Distance(g8) = 19.558
    c: Diameter(g4) = 3.81
    c: Equal(g4,g7)
    c: Equal(g4,g6)
    c: Equal(g4,g5)
FEATURE [PartDesign::Hole] Hole
  BaseFeature = -> Pad007
  Depth = 25
  DepthType = 1
  Diameter = 4.3
  DrillForDepth = false
  DrillPoint = 1
  DrillPointAngle = 118
  HoleCutCountersinkAngle = 82
  HoleCutCustomValues = false
  HoleCutDepth = 0
  HoleCutDiameter = 8.298
  HoleCutType = 2
  ModelActualThread = false
  Profile = -> Sketch012
  Refine = true
  Tapered = false
  TaperedAngle = 90
  ThreadAngle = 0
  ThreadClass = 0
  ThreadCutOffInner = 0
  ThreadCutOffOuter = 0
  ThreadDirection = 0
  ThreadFit = 0
  ThreadPitch = 0
  ThreadSize = 5
  ThreadType = 3
  Threaded = false
FEATURE [Sketcher::SketchObject] Sketch075
  AttachmentOffset = pos=(0,0,4.5) rot=(0,0,1;0rad)
  FullyConstrained = true
  MapMode = 5
  Placement = pos=(0,0,4.5) rot=(0,0,1;0rad)
  Support = -> [XY_Plane006]
  sketch-geometry (1):
    g0: Circle CenterX=0 CenterY=0 CenterZ=0 NormalX=0 NormalY=0 NormalZ=1 AngleXU=0 Radius=4
  constraints (2):
    c: Coincident(g0,g-1)
    c: Diameter(g0) = 8
FEATURE [PartDesign::Pad] Pad048
  BaseFeature = -> Hole
  Direction = (1,1,1)
  Length = 1
  Length2 = 100
  Profile = -> Sketch075
  Type = 0
FEATURE [Sketcher::SketchObject] Sketch088
  AttachmentOffset = pos=(0,0,1) rot=(0,0,1;0rad)
  FullyConstrained = true
  MapMode = 5
  Placement = pos=(0,0,1) rot=(0,0,1;0rad)
  Support = -> [XY_Plane006]
  sketch-geometry (6):
    g0: LineSegment StartX=-27 StartY=0 StartZ=0 EndX=-27 EndY=30 EndZ=0
    g1: LineSegment StartX=-27 StartY=30 StartZ=0 EndX=27 EndY=30 EndZ=0
    g2: LineSegment StartX=27 StartY=30 StartZ=0 EndX=27 EndY=0 EndZ=0
    g3: LineSegment StartX=27 StartY=0 StartZ=0 EndX=26.5 EndY=2.63e-14 EndZ=0
    g4: LineSegment StartX=-26.5 StartY=-1.0088e-12 StartZ=0 EndX=-27 EndY=0 EndZ=0
    g5: ArcOfCircle CenterX=0 CenterY=0 CenterZ=0 NormalX=0 NormalY=0 NormalZ=1 AngleXU=0 Radius=26.5 StartAngle=1e-15 EndAngle=3.14159
  constraints (17):
    c: PointOnObject(g0,g-1)
    c: Vertical(g0)
    c: Coincident(g0,g1)
    c: Coincident(g1,g2)
    c: PointOnObject(g2,g-1)
    c: Coincident(g2,g3)
    c: PointOnObject(g3,g-1)
    c: PointOnObject(g4,g-1)
    c: Coincident(g4,g0)
    c: Coincident(g5,g-1)
    c: Coincident(g5,g4)
    c: Coincident(g5,g3)
    c: Diameter(g5) = 53
    c: DistanceX(g1,g1) = 54
    c: Symmetric(g0,g1,g-2)
    c: Vertical(g2)
    c: DistanceY(g-1,g1) = 30
FEATURE [PartDesign::Pad] Pad054
  BaseFeature = -> Pad048
  Direction = (1,1,1)
  Length = 7
  Length2 = 100
  Profile = -> Sketch088
  Refine = true
  Type = 0
FEATURE [Sketcher::SketchObject] Sketch089
  FullyConstrained = true
  MapMode = 5
  Support = -> [XY_Plane006]
  sketch-geometry (2):
    g0: Circle CenterX=-20 CenterY=25 CenterZ=0 NormalX=0 NormalY=0 NormalZ=1 AngleXU=0 Radius=1.7272
    g1: Circle CenterX=20 CenterY=25 CenterZ=0 NormalX=0 NormalY=0 NormalZ=1 AngleXU=0 Radius=1.7272
  constraints (5):
    c: Diameter(g1) = 3.4544
    c: Equal(g1,g0)
    c: Symmetric(g1,g0,g-2)
    c: DistanceX(g0,g1) = 40
    c: DistanceY(g-1,g1) = 25
FEATURE [PartDesign::Pocket] Pocket028
  BaseFeature = -> Pad054
  Length = 5
  Length2 = 100
  Profile = -> Sketch089
  Refine = true
  Reversed = true
  Type = 1
FEATURE [PartDesign::Body] Body002
  Group = -> [Sketch008,Pad007,Sketch012,Hole,Sketch075,Pad048,Sketch088,Pad054,Sketch089,Pocket028]
  Origin = -> Origin006
  Tip = -> Pocket028
COMPONENT P14 — recipe-attached ("J1_PLATE_2V0", modeled in this document).
Construction recipe (the document's own serialized feature program — sketch geometry with constraints, then the solid features built on it; lengths are millimeters unless a unit is written):

FEATURE [Sketcher::SketchObject] Sketch080
  AttachmentOffset = pos=(0,0,4.5) rot=(0,0,1;0rad)
  FullyConstrained = true
  MapMode = 5
  Placement = pos=(0,0,4.5) rot=(0,0,1;0rad)
  Support = -> [XY_Plane036]
  sketch-geometry (1):
    g0: Circle CenterX=0 CenterY=0 CenterZ=0 NormalX=0 NormalY=0 NormalZ=1 AngleXU=0 Radius=4
  constraints (2):
    c: Coincident(g0,g-1)
    c: Diameter(g0) = 8
FEATURE [Sketcher::SketchObject] Sketch081
  FullyConstrained = true
  MapMode = 5
  Support = -> [XY_Plane036]
  sketch-geometry (6):
    g0: Circle CenterX=-18 CenterY=18 CenterZ=0 NormalX=0 NormalY=0 NormalZ=1 AngleXU=0 Radius=1.7272
    g1: Circle CenterX=17 CenterY=18 CenterZ=0 NormalX=0 NormalY=0 NormalZ=1 AngleXU=0 Radius=1.7272
    g2: LineSegment StartX=-27 StartY=8 StartZ=0 EndX=27 EndY=8 EndZ=0
    g3: LineSegment StartX=-27 StartY=0 StartZ=0 EndX=-27 EndY=28 EndZ=0
    g4: LineSegment StartX=-27 StartY=28 StartZ=0 EndX=27 EndY=28 EndZ=0
    g5: LineSegment StartX=27 StartY=28 StartZ=0 EndX=27 EndY=0 EndZ=0
  constraints (19):
    c: DistanceX(g0,g1) = 35
    c: Horizontal(g2)
    c: DistanceY(g-1,g2) = 8
    c: Equal(g0,g1)
    c: Diameter(g0) = 3.4544
    c: PointOnObject(g3,g-1)
    c: Vertical(g3)
    c: Coincident(g3,g4)
    c: Coincident(g4,g5)
    c: PointOnObject(g5,g-1)
    c: Vertical(g5)
    c: Symmetric(g3,g4,g-2)
    c: PointOnObject(g2,g5)
    c: PointOnObject(g2,g3)
    c: DistanceX(g4,g4) = 54
    c: DistanceY(g5,g5) = 28
    c: DistanceY(g2,g1) = 10
    c: DistanceX(g1,g4) = 10
    c: Horizontal(g0,g1)
FEATURE [Sketcher::SketchObject] Sketch083
  FullyConstrained = true
  MapMode = 5
  Support = -> [XY_Plane036]
  sketch-geometry (2):
    g0: Circle CenterX=0 CenterY=0 CenterZ=0 NormalX=0 NormalY=0 NormalZ=1 AngleXU=0 Radius=3.1
    g1: Circle CenterX=0 CenterY=0 CenterZ=0 NormalX=0 NormalY=0 NormalZ=1 AngleXU=0 Radius=27
  constraints (4):
    c: Diameter(g0) = 6.2
    c: Coincident(g0,g-1)
    c: Coincident(g1,g0)
    c: Diameter(g1) = 54
FEATURE [PartDesign::Pad] Pad050
  AllowMultiFace = false
  Direction = (1,1,1)
  Length = 8
  Length2 = 100
  Profile = -> Sketch083
  Type = 0
FEATURE [Sketcher::SketchObject] Sketch084
  AttachmentOffset = pos=(0,0,8) rot=(0,0,1;0rad)
  FullyConstrained = true
  MapMode = 5
  Placement = pos=(0,0,8) rot=(0,0,1;0rad)
  Support = -> [XY_Plane036]
  sketch-geometry (8):
    g0: LineSegment StartX=-8 StartY=8 StartZ=0 EndX=8 EndY=8 EndZ=0
    g1: LineSegment StartX=8 StartY=8 StartZ=0 EndX=8 EndY=-8 EndZ=0
    g2: LineSegment StartX=8 StartY=-8 StartZ=0 EndX=-8 EndY=-8 EndZ=0
    g3: LineSegment StartX=-8 StartY=-8 StartZ=0 EndX=-8 EndY=8 EndZ=0
    g4: Circle CenterX=-8 CenterY=8 CenterZ=0 NormalX=0 NormalY=0 NormalZ=1 AngleXU=0 Radius=2.25
    g5: Circle CenterX=8 CenterY=8 CenterZ=0 NormalX=0 NormalY=0 NormalZ=1 AngleXU=0 Radius=2.25
    g6: Circle CenterX=8 CenterY=-8 CenterZ=0 NormalX=0 NormalY=0 NormalZ=1 AngleXU=0 Radius=2.25
    g7: Circle CenterX=-8 CenterY=-8 CenterZ=0 NormalX=0 NormalY=0 NormalZ=1 AngleXU=0 Radius=2.25
  constraints (18):
    c: Coincident(g0,g1)
    c: Coincident(g1,g2)
    c: Coincident(g2,g3)
    c: Coincident(g3,g0)
    c: Horizontal(g2)
    c: Vertical(g1)
    c: Symmetric(g0,g0,g-2)
    c: Symmetric(g0,g2,g-1)
    c: Equal(g3,g0)
    c: Coincident(g4,g0)
    c: Coincident(g5,g0)
    c: Coincident(g6,g1)
    c: Coincident(g7,g2)
    c: Diameter(g4) = 4.5
    c: Equal(g4,g7)
    c: Equal(g4,g6)
    c: Equal(g4,g5)
    c: DistanceY(g1,g1) = 16
FEATURE [PartDesign::Hole] Hole003
  BaseFeature = -> Pad050
  Depth = 25
  DepthType = 1
  Diameter = 4.5
  DrillForDepth = false
  DrillPoint = 1
  DrillPointAngle = 118
  HoleCutCountersinkAngle = 90
  HoleCutCustomValues = false
  HoleCutDepth = 0
  HoleCutDiameter = 9
  HoleCutType = 7
  ModelActualThread = false
  Profile = -> Sketch084
  Refine = true
  Tapered = false
  TaperedAngle = 90
  ThreadAngle = 0
  ThreadClass = 0
  ThreadCutOffInner = 0
  ThreadCutOffOuter = 0
  ThreadDirection = 0
  ThreadFit = 0
  ThreadPitch = 0
  ThreadSize = 11
  ThreadType = 1
  Threaded = false
FEATURE [PartDesign::Pad] Pad051
  BaseFeature = -> Hole003
  Direction = (1,1,1)
  Length = 1
  Length2 = 100
  Profile = -> Sketch080
  Type = 0
FEATURE [Sketcher::SketchObject] Sketch085
  AttachmentOffset = pos=(0,0,1) rot=(0,0,1;0rad)
  FullyConstrained = true
  MapMode = 5
  Placement = pos=(0,0,1) rot=(0,0,1;0rad)
  Support = -> [XY_Plane036]
  sketch-geometry (7):
    g0: LineSegment StartX=-27 StartY=0 StartZ=0 EndX=-27 EndY=28 EndZ=0
    g1: LineSegment StartX=-27 StartY=28 StartZ=0 EndX=27 EndY=28 EndZ=0
    g2: LineSegment StartX=27 StartY=28 StartZ=0 EndX=27 EndY=0 EndZ=0
    g3: LineSegment StartX=27 StartY=0 StartZ=0 EndX=25 EndY=0 EndZ=0
    g4: LineSegment StartX=-25 StartY=3.1e-15 StartZ=0 EndX=-27 EndY=0 EndZ=0
    g5: ArcOfCircle CenterX=0 CenterY=0 CenterZ=0 NormalX=0 NormalY=0 NormalZ=1 AngleXU=0 Radius=25 StartAngle=0 EndAngle=3.14159
    g6: LineSegment StartX=-27 StartY=8 StartZ=0 EndX=27 EndY=8 EndZ=0
  constraints (21):
    c: PointOnObject(g0,g-1)
    c: Vertical(g0)
    c: Coincident(g1,g0)
    c: Coincident(g2,g1)
    c: PointOnObject(g2,g-1)
    c: Coincident(g3,g2)
    c: PointOnObject(g3,g-1)
    c: PointOnObject(g4,g-1)
    c: Coincident(g4,g0)
    c: Coincident(g5,g-1)
    c: Coincident(g5,g4)
    c: Coincident(g5,g3)
    c: Vertical(g2)
    c: DistanceX(g1,g1) = 54
    c: Symmetric(g0,g1,g-2)
    c: Diameter(g5) = 50
    c: PointOnObject(g6,g0)
    c: PointOnObject(g6,g2)
    c: Horizontal(g6)
    c: DistanceY(g6,g1) = 20
    c: DistanceY(g-1,g6) = 8
FEATURE [PartDesign::Pad] Pad052
  BaseFeature = -> Pad051
  Direction = (1,1,1)
  Length = 7
  Length2 = 100
  Profile = -> Sketch085
  Refine = true
  Type = 0
FEATURE [PartDesign::Pocket] Pocket026
  BaseFeature = -> Pad052
  Length = 5
  Length2 = 100
  Profile = -> Sketch081
  Refine = true
  Reversed = true
  Type = 1
FEATURE [PartDesign::Body] Body017
  Group = -> [Sketch083,Pad050,Sketch084,Hole003,Sketch080,Pad051,Sketch081,Sketch085,Pad052,Pocket026]
  Origin = -> Origin035
  Tip = -> Pocket026
COMPONENT P15 — recipe-attached ("J2_PLATE_2V0", modeled in this document).
Construction recipe (the document's own serialized feature program — sketch geometry with constraints, then the solid features built on it; lengths are millimeters unless a unit is written):

FEATURE [Sketcher::SketchObject] Sketch092
  AttachmentOffset = pos=(0,0,8) rot=(0,0,1;0rad)
  FullyConstrained = true
  MapMode = 5
  Placement = pos=(0,0,8) rot=(0,0,1;0rad)
  Support = -> [XY_Plane038]
  expr: Constraints[16] = <<var>>.hubHoleD
  expr: Constraints[15] = <<var>>.hubHolePD
  sketch-geometry (9):
    g0: LineSegment StartX=-6.9148 StartY=6.9148 StartZ=0 EndX=6.9148 EndY=6.9148 EndZ=0
    g1: LineSegment StartX=6.9148 StartY=6.9148 StartZ=0 EndX=6.9148 EndY=-6.9148 EndZ=0
    g2: LineSegment StartX=6.9148 StartY=-6.9148 StartZ=0 EndX=-6.9148 EndY=-6.9148 EndZ=0
    g3: LineSegment StartX=-6.9148 StartY=-6.9148 StartZ=0 EndX=-6.9148 EndY=6.9148 EndZ=0
    g4: Circle CenterX=-6.9148 CenterY=6.9148 CenterZ=0 NormalX=0 NormalY=0 NormalZ=1 AngleXU=0 Radius=1.905
    g5: Circle CenterX=6.9148 CenterY=6.9148 CenterZ=0 NormalX=0 NormalY=0 NormalZ=1 AngleXU=0 Radius=1.905
    g6: Circle CenterX=6.9148 CenterY=-6.9148 CenterZ=0 NormalX=0 NormalY=0 NormalZ=1 AngleXU=0 Radius=1.905
    g7: Circle CenterX=-6.9148 CenterY=-6.9148 CenterZ=0 NormalX=0 NormalY=0 NormalZ=1 AngleXU=0 Radius=1.905
    g8: LineSegment StartX=-6.9148 StartY=6.9148 StartZ=0 EndX=6.9148 EndY=-6.9148 EndZ=0
  constraints (20):
    c: Coincident(g0,g1)
    c: Coincident(g1,g2)
    c: Coincident(g2,g3)
    c: Coincident(g3,g0)
    c: Horizontal(g2)
    c: Vertical(g1)
    c: Symmetric(g0,g0,g-2)
    c: Symmetric(g0,g2,g-1)
    c: Equal(g3,g0)
    c: Coincident(g4,g0)
    c: Coincident(g5,g0)
    c: Coincident(g6,g1)
    c: Coincident(g7,g2)
    c: Coincident(g8,g4)
    c: Coincident(g8,g6)
    c: Distance(g8) = 19.558
    c: Diameter(g4) = 3.81
    c: Equal(g4,g7)
    c: Equal(g4,g6)
    c: Equal(g4,g5)
FEATURE [Sketcher::SketchObject] Sketch093
  AttachmentOffset = pos=(0,0,4.5) rot=(0,0,1;0rad)
  FullyConstrained = true
  MapMode = 5
  Placement = pos=(0,0,4.5) rot=(0,0,1;0rad)
  Support = -> [XY_Plane038]
  sketch-geometry (1):
    g0: Circle CenterX=0 CenterY=0 CenterZ=0 NormalX=0 NormalY=0 NormalZ=1 AngleXU=0 Radius=4
  constraints (2):
    c: Coincident(g0,g-1)
    c: Diameter(g0) = 8
FEATURE [Sketcher::SketchObject] Sketch094
  AttachmentOffset = pos=(0,0,2) rot=(0,0,1;0rad)
  FullyConstrained = true
  MapMode = 5
  Placement = pos=(0,0,2) rot=(0,0,1;0rad)
  Support = -> [XY_Plane038]
  sketch-geometry (6):
    g0: Circle CenterX=-12 CenterY=18.3 CenterZ=0 NormalX=0 NormalY=0 NormalZ=1 AngleXU=0 Radius=1.75
    g1: Circle CenterX=12 CenterY=18.3 CenterZ=0 NormalX=0 NormalY=0 NormalZ=1 AngleXU=0 Radius=1.75
    g2: LineSegment StartX=-22 StartY=8 StartZ=0 EndX=22 EndY=8 EndZ=0
    g3: LineSegment StartX=-22 StartY=0 StartZ=0 EndX=-22 EndY=28.6 EndZ=0
    g4: LineSegment StartX=-22 StartY=28.6 StartZ=0 EndX=22 EndY=28.6 EndZ=0
    g5: LineSegment StartX=22 StartY=28.6 StartZ=0 EndX=22 EndY=0 EndZ=0
  constraints (20):
    c: Horizontal(g2)
    c: DistanceY(g-1,g2) = 8
    c: Equal(g0,g1)
    c: Diameter(g0) = 3.5
    c: PointOnObject(g3,g-1)
    c: Vertical(g3)
    c: Coincident(g3,g4)
    c: Coincident(g4,g5)
    c: PointOnObject(g5,g-1)
    c: Vertical(g5)
    c: Symmetric(g3,g4,g-2)
    c: PointOnObject(g2,g5)
    c: PointOnObject(g2,g3)
    c: DistanceX(g4,g4) = 44
    c: DistanceY(g5,g5) = 28.6
    c: DistanceY(g2,g1) = 10.3
    c: DistanceX(g1,g4) = 10
    c: Horizontal(g0,g1)
    c: DistanceX(g3,g0) = 10
    c: DistanceX(g0,g1) = 24
FEATURE [Sketcher::SketchObject] Sketch095
  AttachmentOffset = pos=(0,0,1) rot=(0,0,1;0rad)
  FullyConstrained = true
  MapMode = 5
  Placement = pos=(0,0,1) rot=(0,0,1;0rad)
  Support = -> [XY_Plane038]
  sketch-geometry (7):
    g0: LineSegment StartX=-22 StartY=0 StartZ=0 EndX=-22 EndY=28.6 EndZ=0
    g1: LineSegment StartX=-22 StartY=28.6 StartZ=0 EndX=22 EndY=28.6 EndZ=0
    g2: LineSegment StartX=22 StartY=28.6 StartZ=0 EndX=22 EndY=0 EndZ=0
    g3: LineSegment StartX=22 StartY=0 StartZ=0 EndX=21 EndY=-7.46e-14 EndZ=0
    g4: LineSegment StartX=-21 StartY=3.8635e-12 StartZ=0 EndX=-22 EndY=0 EndZ=0
    g5: ArcOfCircle CenterX=0 CenterY=0 CenterZ=0 NormalX=0 NormalY=0 NormalZ=1 AngleXU=0 Radius=21 StartAngle=-3.6e-15 EndAngle=3.14159
    g6: LineSegment StartX=-22 StartY=8 StartZ=0 EndX=22 EndY=8 EndZ=0
  constraints (21):
    c: PointOnObject(g0,g-1)
    c: Vertical(g0)
    c: Coincident(g1,g0)
    c: Coincident(g2,g1)
    c: PointOnObject(g2,g-1)
    c: Coincident(g3,g2)
    c: PointOnObject(g3,g-1)
    c: PointOnObject(g4,g-1)
    c: Coincident(g4,g0)
    c: Coincident(g5,g-1)
    c: Coincident(g5,g4)
    c: Coincident(g5,g3)
    c: Vertical(g2)
    c: DistanceX(g1,g1) = 44
    c: Symmetric(g0,g1,g-2)
    c: Diameter(g5) = 42
    c: PointOnObject(g6,g0)
    c: PointOnObject(g6,g2)
    c: Horizontal(g6)
    c: DistanceY(g6,g1) = 20.6
    c: DistanceY(g-1,g6) = 8
FEATURE [Sketcher::SketchObject] Sketch096
  FullyConstrained = true
  MapMode = 5
  Support = -> [XY_Plane038]
  sketch-geometry (2):
    g0: Circle CenterX=0 CenterY=0 CenterZ=0 NormalX=0 NormalY=0 NormalZ=1 AngleXU=0 Radius=3.1
    g1: Circle CenterX=0 CenterY=0 CenterZ=0 NormalX=0 NormalY=0 NormalZ=1 AngleXU=0 Radius=22
  constraints (4):
    c: Diameter(g0) = 6.2
    c: Coincident(g0,g-1)
    c: Coincident(g1,g0)
    c: Diameter(g1) = 44
FEATURE [PartDesign::Pad] Pad057
  AllowMultiFace = false
  Direction = (1,1,1)
  Length = 8
  Length2 = 100
  Profile = -> Sketch096
  Type = 0
FEATURE [PartDesign::Hole] Hole005
  BaseFeature = -> Pad057
  Depth = 25
  DepthType = 1
  Diameter = 4.3
  DrillForDepth = false
  DrillPoint = 1
  DrillPointAngle = 118
  HoleCutCountersinkAngle = 82
  HoleCutCustomValues = false
  HoleCutDepth = 0
  HoleCutDiameter = 8.298
  HoleCutType = 2
  ModelActualThread = false
  Profile = -> Sketch092
  Refine = true
  Tapered = false
  TaperedAngle = 90
  ThreadAngle = 0
  ThreadClass = 0
  ThreadCutOffInner = 0
  ThreadCutOffOuter = 0
  ThreadDirection = 0
  ThreadFit = 0
  ThreadPitch = 0
  ThreadSize = 5
  ThreadType = 3
  Threaded = false
FEATURE [PartDesign::Pad] Pad058
  BaseFeature = -> Hole005
  Direction = (1,1,1)
  Length = 1
  Length2 = 100
  Profile = -> Sketch093
  Type = 0
FEATURE [PartDesign::Pad] Pad059
  BaseFeature = -> Pad058
  Direction = (1,1,1)
  Length = 7
  Length2 = 100
  Profile = -> Sketch095
  Refine = true
  Type = 0
FEATURE [PartDesign::Pocket] Pocket029
  BaseFeature = -> Pad059
  Length = 5
  Length2 = 100
  Profile = -> Sketch094
  Refine = true
  Reversed = true
  Type = 1
FEATURE [PartDesign::Body] Body018
  Group = -> [Sketch096,Pad057,Sketch092,Hole005,Sketch093,Pad058,Sketch094,Sketch095,Pad059,Pocket029]
  Origin = -> Origin038
  Tip = -> Pocket029
COMPONENT P16 — recipe-attached ("RADIUS_2V0", modeled in this document).
Construction recipe (the document's own serialized feature program — sketch geometry with constraints, then the solid features built on it; lengths are millimeters unless a unit is written):

FEATURE [Sketcher::SketchObject] Sketch050
  FullyConstrained = true
  MapMode = 5
  Support = -> [XY_Plane024]
  expr: Constraints[39] = <<var>>.humerusW
  sketch-geometry (16):
    g0: LineSegment StartX=5.15937 StartY=-10.3187 StartZ=0 EndX=5.15937 EndY=10.3187 EndZ=0
    g1: LineSegment StartX=5.15937 StartY=10.3187 StartZ=0 EndX=-5.15937 EndY=10.3187 EndZ=0
    g2: LineSegment StartX=-5.15937 StartY=10.3187 StartZ=0 EndX=-5.15937 EndY=5.55625 EndZ=0
    g3: LineSegment StartX=-5.15937 StartY=5.55625 StartZ=0 EndX=-2.15937 EndY=5.55625 EndZ=0
    g4: LineSegment StartX=-2.15937 StartY=5.55625 StartZ=0 EndX=-2.15937 EndY=6.55625 EndZ=0
    g5: LineSegment StartX=-2.15937 StartY=6.55625 StartZ=0 EndX=-4.15937 EndY=6.55625 EndZ=0
    g6: LineSegment StartX=-4.15937 StartY=6.55625 StartZ=0 EndX=-4.15937 EndY=9.31875 EndZ=0
    g7: LineSegment StartX=-4.15937 StartY=9.31875 StartZ=0 EndX=3.63537 EndY=9.31875 EndZ=0
    g8: LineSegment StartX=3.63537 StartY=9.31875 StartZ=0 EndX=3.63537 EndY=-9.31875 EndZ=0
    g9: LineSegment StartX=3.63537 StartY=-9.31875 StartZ=0 EndX=-4.15937 EndY=-9.31875 EndZ=0
    g10: LineSegment StartX=-4.15937 StartY=-9.31875 StartZ=0 EndX=-4.15937 EndY=-6.55625 EndZ=0
    g11: LineSegment StartX=-4.15937 StartY=-6.55625 StartZ=0 EndX=-2.15937 EndY=-6.55625 EndZ=0
    g12: LineSegment StartX=-2.15937 StartY=-6.55625 StartZ=0 EndX=-2.15937 EndY=-5.55625 EndZ=0
    g13: LineSegment StartX=-2.15937 StartY=-5.55625 StartZ=0 EndX=-5.15937 EndY=-5.55625 EndZ=0
    g14: LineSegment StartX=-5.15937 StartY=-5.55625 StartZ=0 EndX=-5.15937 EndY=-10.3187 EndZ=0
    g15: LineSegment StartX=-5.15937 StartY=-10.3187 StartZ=0 EndX=5.15937 EndY=-10.3187 EndZ=0
  constraints (45):
    c: Coincident(g0,g1)
    c: Coincident(g1,g2)
    c: Vertical(g2)
    c: Coincident(g2,g3)
    c: Coincident(g3,g4)
    c: Coincident(g4,g5)
    c: Horizontal(g5)
    c: Coincident(g5,g6)
    c: Coincident(g6,g7)
    c: Horizontal(g7)
    c: Coincident(g7,g8)
    c: Vertical(g8)
    c: Coincident(g8,g9)
    c: Horizontal(g9)
    c: Coincident(g9,g10)
    c: Vertical(g10)
    c: Coincident(g10,g11)
    c: Horizontal(g11)
    c: Coincident(g11,g12)
    c: Vertical(g12)
    c: Coincident(g12,g13)
    c: Horizontal(g13)
    c: Coincident(g13,g14)
    c: Vertical(g14)
    c: Coincident(g14,g15)
    c: Coincident(g15,g0)
    c: DistanceX(g7,g0) = 1.524
    c: DistanceY(g6,g1) = 1
    c: Vertical(g6)
    c: Horizontal(g3)
    c: Vertical(g4)
    c: DistanceY(g4,g4) = 1
    c: DistanceX(g2,g5) = 1
    c: Symmetric(g2,g13,g-1)
    c: Equal(g3,g13)
    c: Equal(g12,g4)
    c: Equal(g2,g14)
    c: Equal(g10,g6)
    c: Equal(g11,g5)
    c: DistanceY(g0,g0) = 20.6375
    c: DistanceX(g15,g15) = 10.3187
    c: DistanceY(g13,g2) = 11.1125
    c: Symmetric(g1,g0,g-2)
    c: Symmetric(g0,g0,g-1)
    c: DistanceX(g3,g3) = 3
FEATURE [PartDesign::Pad] Pad031
  AllowMultiFace = false
  Direction = (1,1,1)
  Length = 304.8
  Length2 = 100
  Profile = -> Sketch050
  Type = 0
FEATURE [Sketcher::SketchObject] Sketch049
  ExternalGeometry = -> [Pad031]
  FullyConstrained = true
  MapMode = 5
  Placement = pos=(5.15937,0,0) rot=(0.57735,0.57735,0.57735;2.0944rad)
  Support = -> [Pad031]
  sketch-geometry (4):
    g0: Circle CenterX=0 CenterY=10 CenterZ=0 NormalX=0 NormalY=0 NormalZ=1 AngleXU=0 Radius=2.25
    g1: Circle CenterX=0 CenterY=34 CenterZ=0 NormalX=0 NormalY=0 NormalZ=1 AngleXU=0 Radius=2.25
    g2: Circle CenterX=0 CenterY=294.8 CenterZ=0 NormalX=0 NormalY=0 NormalZ=1 AngleXU=0 Radius=2.25
    g3: Circle CenterX=0 CenterY=262.8 CenterZ=0 NormalX=0 NormalY=0 NormalZ=1 AngleXU=0 Radius=2.25
  constraints (12):
    c: PointOnObject(g0,g-2)
    c: PointOnObject(g1,g-2)
    c: Equal(g1,g0)
    c: DistanceY(g0,g1) = 24
    c: DistanceY(g-1,g0) = 10
    c: PointOnObject(g3,g-2)
    c: Diameter(g2) = 4.5
    c: Equal(g2,g3)
    c: PointOnObject(g2,g-2)
    c: DistanceY(g3,g2) = 32
    c: DistanceY(g2,g-3) = 10
    c: Equal(g1,g2)
FEATURE [PartDesign::Pocket] Pocket016
  AllowMultiFace = false
  BaseFeature = -> Pad031
  Length = 5
  Length2 = 100
  Profile = -> Sketch049
  Type = 0
FEATURE [PartDesign::Body] Body011  label="RADIUS_1_0"
  Group = -> [Sketch050,Pad031,Sketch049,Pocket016]
  Origin = -> Origin024
  Tip = -> Pocket016
COMPONENT P17 — recipe-attached ("RISER_2V0", modeled in this document).
Construction recipe (the document's own serialized feature program — sketch geometry with constraints, then the solid features built on it; lengths are millimeters unless a unit is written):

FEATURE [Sketcher::SketchObject] Sketch002
  AttachmentOffset = pos=(0,0,70) rot=(0,0,1;0rad)
  FullyConstrained = true
  MapMode = 5
  Placement = pos=(0,0,70) rot=(0,0,1;0rad)
  Support = -> [XY_Plane002]
  expr: Constraints[22] = <<var>>.riserHoleD
  expr: Constraints[27] = <<var>>.riserOD - 1
  expr: Constraints[12] = <<var>>.riserOD - 15
  expr: Constraints[13] = <<var>>.riserOD
  sketch-geometry (13):
    g0: LineSegment StartX=-28 StartY=35.5 StartZ=0 EndX=28 EndY=35.5 EndZ=0
    g1: LineSegment StartX=35.5 StartY=28 StartZ=0 EndX=35.5 EndY=-28 EndZ=0
    g2: LineSegment StartX=28 StartY=-35.5 StartZ=0 EndX=-28 EndY=-35.5 EndZ=0
    g3: LineSegment StartX=-35.5 StartY=-28 StartZ=0 EndX=-35.5 EndY=28 EndZ=0
    g4: ArcOfCircle CenterX=-28 CenterY=28 CenterZ=0 NormalX=0 NormalY=0 NormalZ=1 AngleXU=0 Radius=7.5 StartAngle=1.5708 EndAngle=3.14159
    g5: ArcOfCircle CenterX=28 CenterY=28 CenterZ=0 NormalX=0 NormalY=0 NormalZ=1 AngleXU=0 Radius=7.5 StartAngle=0 EndAngle=1.5708
    g6: ArcOfCircle CenterX=28 CenterY=-28 CenterZ=0 NormalX=0 NormalY=0 NormalZ=1 AngleXU=0 Radius=7.5 StartAngle=4.71239 EndAngle=6.28319
    g7: ArcOfCircle CenterX=-28 CenterY=-28 CenterZ=0 NormalX=0 NormalY=0 NormalZ=1 AngleXU=0 Radius=7.5 StartAngle=3.14159 EndAngle=4.71239
    g8: Circle CenterX=-28 CenterY=28 CenterZ=0 NormalX=0 NormalY=0 NormalZ=1 AngleXU=0 Radius=2.25
    g9: Circle CenterX=28 CenterY=28 CenterZ=0 NormalX=0 NormalY=0 NormalZ=1 AngleXU=0 Radius=2.25
    g10: Circle CenterX=28 CenterY=-28 CenterZ=0 NormalX=0 NormalY=0 NormalZ=1 AngleXU=0 Radius=2.25
    g11: Circle CenterX=-28 CenterY=-28 CenterZ=0 NormalX=0 NormalY=0 NormalZ=1 AngleXU=0 Radius=2.25
    g12: Circle CenterX=0 CenterY=0 CenterZ=0 NormalX=0 NormalY=0 NormalZ=1 AngleXU=0 Radius=35
  constraints (28):
    c: Horizontal(g0)
    c: Horizontal(g2)
    c: Vertical(g1)
    c: Vertical(g3)
    c: Tangent(g0,g4) = 1.5708
    c: Tangent(g3,g4) = 1.5708
    c: Tangent(g0,g5) = 1.5708
    c: Tangent(g1,g5) = 1.5708
    c: Tangent(g1,g6) = 1.5708
    c: Tangent(g2,g6) = 1.5708
    c: Tangent(g3,g7) = 1.5708
    c: Tangent(g2,g7) = 1.5708
    c: DistanceX(g4,g5) = 56
    c: DistanceX(g3,g1) = 71
    c: Equal(g7,g6)
    c: Symmetric(g4,g5,g-2)
    c: Symmetric(g4,g7,g-1)
    c: Equal(g3,g0)
    c: Coincident(g8,g4)
    c: Coincident(g9,g5)
    c: Coincident(g10,g6)
    c: Coincident(g11,g7)
    c: Diameter(g11) = 4.5
    c: Equal(g11,g8)
    c: Equal(g11,g9)
    c: Equal(g11,g10)
    c: Coincident(g12,g-1)
    c: Diameter(g12) = 70
FEATURE [Sketcher::SketchObject] Sketch003
  FullyConstrained = true
  MapMode = 5
  Placement = pos=(0,0,0) rot=(1,0,0;1.5708rad)
  Support = -> [XZ_Plane002]
  sketch-geometry (8):
    g0: LineSegment StartX=0 StartY=64.8205 StartZ=0 EndX=-10 EndY=47.5 EndZ=0
    g1: LineSegment StartX=-10 StartY=47.5 StartZ=0 EndX=-10 EndY=27.5 EndZ=0
    g2: LineSegment StartX=-10 StartY=27.5 StartZ=0 EndX=0 EndY=10.1795 EndZ=0
    g3: LineSegment StartX=0 StartY=10.1795 StartZ=0 EndX=10 EndY=27.5 EndZ=0
    g4: LineSegment StartX=10 StartY=27.5 StartZ=0 EndX=10 EndY=47.5 EndZ=0
    g5: LineSegment StartX=10 StartY=47.5 StartZ=0 EndX=0 EndY=64.8205 EndZ=0
    g6: GeomPoint X=0 Y=37.5 Z=0
    g7: LineSegment StartX=-10 StartY=47.5 StartZ=0 EndX=10 EndY=27.5 EndZ=0
  constraints (21):
    c: PointOnObject(g0,g-2)
    c: Coincident(g0,g1)
    c: Vertical(g1)
    c: Coincident(g1,g2)
    c: PointOnObject(g2,g-2)
    c: Coincident(g2,g3)
    c: Coincident(g3,g4)
    c: Vertical(g4)
    c: Coincident(g4,g5)
    c: Coincident(g5,g0)
    c: Symmetric(g0,g4,g-2)
    c: Equal(g1,g4)
    c: Angle(g0,g5) = 1.0472
    c: DistanceX(g0,g4) = 20
    c: PointOnObject(g6,g-2)
    c: Coincident(g7,g0)
    c: Coincident(g7,g3)
    c: PointOnObject(g6,g7)
    c: DistanceY(g-1,g6) = 37.5
    c: Equal(g2,g0)
    c: DistanceY(g1,g1) = 20
FEATURE [Sketcher::SketchObject] Sketch001
  FullyConstrained = true
  MapMode = 5
  Support = -> [XY_Plane002]
  expr: Constraints[22] = <<var>>.riserHoleD
  expr: Constraints[27] = Variables.riserOD - 1
  expr: Constraints[12] = Variables.riserOD - 15
  expr: Constraints[13] = Variables.riserOD
  sketch-geometry (13):
    g0: LineSegment StartX=-28 StartY=35.5 StartZ=0 EndX=28 EndY=35.5 EndZ=0
    g1: LineSegment StartX=35.5 StartY=28 StartZ=0 EndX=35.5 EndY=-28 EndZ=0
    g2: LineSegment StartX=28 StartY=-35.5 StartZ=0 EndX=-28 EndY=-35.5 EndZ=0
    g3: LineSegment StartX=-35.5 StartY=-28 StartZ=0 EndX=-35.5 EndY=28 EndZ=0
    g4: ArcOfCircle CenterX=-28 CenterY=28 CenterZ=0 NormalX=0 NormalY=0 NormalZ=1 AngleXU=0 Radius=7.5 StartAngle=1.5708 EndAngle=3.14159
    g5: ArcOfCircle CenterX=28 CenterY=28 CenterZ=0 NormalX=0 NormalY=0 NormalZ=1 AngleXU=0 Radius=7.5 StartAngle=1e-16 EndAngle=1.5708
    g6: ArcOfCircle CenterX=28 CenterY=-28 CenterZ=0 NormalX=0 NormalY=0 NormalZ=1 AngleXU=0 Radius=7.5 StartAngle=4.71239 EndAngle=6.28319
    g7: ArcOfCircle CenterX=-28 CenterY=-28 CenterZ=0 NormalX=0 NormalY=0 NormalZ=1 AngleXU=0 Radius=7.5 StartAngle=3.14159 EndAngle=4.71239
    g8: Circle CenterX=-28 CenterY=28 CenterZ=0 NormalX=0 NormalY=0 NormalZ=1 AngleXU=0 Radius=2.25
    g9: Circle CenterX=28 CenterY=28 CenterZ=0 NormalX=0 NormalY=0 NormalZ=1 AngleXU=0 Radius=2.25
    g10: Circle CenterX=28 CenterY=-28 CenterZ=0 NormalX=0 NormalY=0 NormalZ=1 AngleXU=0 Radius=2.25
    g11: Circle CenterX=-28 CenterY=-28 CenterZ=0 NormalX=0 NormalY=0 NormalZ=1 AngleXU=0 Radius=2.25
    g12: Circle CenterX=0 CenterY=0 CenterZ=0 NormalX=0 NormalY=0 NormalZ=1 AngleXU=0 Radius=35
  constraints (28):
    c: Horizontal(g0)
    c: Horizontal(g2)
    c: Vertical(g1)
    c: Vertical(g3)
    c: Tangent(g0,g4) = 1.5708
    c: Tangent(g3,g4) = 1.5708
    c: Tangent(g0,g5) = 1.5708
    c: Tangent(g1,g5) = 1.5708
    c: Tangent(g1,g6) = 1.5708
    c: Tangent(g2,g6) = 1.5708
    c: Tangent(g3,g7) = 1.5708
    c: Tangent(g2,g7) = 1.5708
    c: DistanceX(g4,g5) = 56
    c: DistanceX(g3,g1) = 71
    c: Equal(g7,g6)
    c: Symmetric(g4,g5,g-2)
    c: Symmetric(g4,g7,g-1)
    c: Equal(g3,g0)
    c: Coincident(g8,g4)
    c: Coincident(g9,g5)
    c: Coincident(g10,g6)
    c: Coincident(g11,g7)
    c: Diameter(g11) = 4.5
    c: Equal(g11,g8)
    c: Equal(g11,g9)
    c: Equal(g11,g10)
    c: Coincident(g12,g-1)
    c: Diameter(g12) = 70
FEATURE [Sketcher::SketchObject] Sketch
  FullyConstrained = true
  MapMode = 5
  Support = -> [XY_Plane002]
  sketch-geometry (7):
    g0: Circle CenterX=0 CenterY=0 CenterZ=0 NormalX=0 NormalY=0 NormalZ=1 AngleXU=0 Radius=32.5
    g1: Circle CenterX=0 CenterY=0 CenterZ=0 NormalX=0 NormalY=0 NormalZ=1 AngleXU=0 Radius=35.5
    g2: LineSegment StartX=-21.15 StartY=21.15 StartZ=0 EndX=21.15 EndY=21.15 EndZ=0
    g3: LineSegment StartX=21.15 StartY=21.15 StartZ=0 EndX=21.15 EndY=-21.15 EndZ=0
    g4: LineSegment StartX=21.15 StartY=-21.15 StartZ=0 EndX=-21.15 EndY=-21.15 EndZ=0
    g5: LineSegment StartX=-21.15 StartY=-21.15 StartZ=0 EndX=-21.15 EndY=21.15 EndZ=0
    g6: Circle CenterX=0 CenterY=0 CenterZ=0 NormalX=0 NormalY=0 NormalZ=1 AngleXU=0 Radius=29.9106
  constraints (17):
    c: Coincident(g0,g-1)
    c: Coincident(g1,g0)
    c: Diameter(g1) = 71
    c: Diameter(g0) = 65
    c: Coincident(g2,g3)
    c: Coincident(g3,g4)
    c: Coincident(g4,g5)
    c: Coincident(g5,g2)
    c: Horizontal(g4)
    c: Vertical(g3)
    c: Symmetric(g2,g2,g-2)
    c: Equal(g2,g5)
    c: Symmetric(g2,g4,g-1)
    c: DistanceX(g2,g2) = 42.3
    c: Coincident(g6,g0)
    c: Diameter(g6) = 59.8212
    c: PointOnObject(g3,g6)
FEATURE [PartDesign::Pad] Pad
  Direction = (1,1,1)
  Length = 75
  Length2 = 100
  Profile = -> Sketch
  Refine = true
  Type = 0
FEATURE [PartDesign::Pad] Pad001
  BaseFeature = -> Pad
  Direction = (1,1,1)
  Length = 5
  Length2 = 100
  Profile = -> Sketch001
  Refine = true
  Type = 0
FEATURE [PartDesign::Pad] Pad002
  BaseFeature = -> Pad001
  Direction = (1,1,1)
  Length = 5
  Length2 = 100
  Profile = -> Sketch002
  Refine = true
  Type = 0
FEATURE [PartDesign::Pocket] Pocket
  BaseFeature = -> Pad002
  Length = 5
  Length2 = 100
  Midplane = true
  Profile = -> Sketch003
  Refine = true
  Type = 1
FEATURE [PartDesign::PolarPattern] PolarPattern
  Angle = 90
  Axis = -> Sketch003 [V_Axis]
  BaseFeature = -> Pocket
  Occurrences = 2
  Originals = -> [Pocket]
  Refine = true
FEATURE [PartDesign::Body] Body
  Group = -> [Sketch,Pad,Sketch001,Sketch002,Pad001,Pad002,Sketch003,Pocket,PolarPattern]
  Origin = -> Origin002
  Tip = -> PolarPattern
COMPONENT P18 — recipe-attached ("J2_TENSIONER_2V0", modeled in this document).
Construction recipe (the document's own serialized feature program — sketch geometry with constraints, then the solid features built on it; lengths are millimeters unless a unit is written):

FEATURE [PartDesign::CoordinateSystem] LCS_0008
  AttacherType = Attacher::AttachEngine3D
  MapMode = 2
  Support = -> [X_Axis017]
FEATURE [Sketcher::SketchObject] Sketch033
  FullyConstrained = true
  MapMode = 5
  Support = -> [XY_Plane017]
  sketch-geometry (7):
    g0: LineSegment StartX=35 StartY=10 StartZ=0 EndX=35 EndY=-10 EndZ=0
    g1: LineSegment StartX=35 StartY=-10 StartZ=0 EndX=0 EndY=-10 EndZ=0
    g2: LineSegment StartX=0 StartY=-10 StartZ=0 EndX=0 EndY=35 EndZ=0
    g3: LineSegment StartX=0 StartY=35 StartZ=0 EndX=10 EndY=35 EndZ=0
    g4: LineSegment StartX=10 StartY=35 StartZ=0 EndX=35 EndY=10 EndZ=0
    g5: Circle CenterX=15 CenterY=0 CenterZ=0 NormalX=0 NormalY=0 NormalZ=1 AngleXU=0 Radius=2.25
    g6: Circle CenterX=30 CenterY=0 CenterZ=0 NormalX=0 NormalY=0 NormalZ=1 AngleXU=0 Radius=2.25
  constraints (21):
    c: Coincident(g0,g1)
    c: Horizontal(g1)
    c: Coincident(g1,g2)
    c: PointOnObject(g2,g-2)
    c: Vertical(g2)
    c: Coincident(g2,g3)
    c: Horizontal(g3)
    c: Coincident(g3,g4)
    c: Coincident(g4,g0)
    c: DistanceX(g3,g3) = 10
    c: PointOnObject(g5,g-1)
    c: PointOnObject(g6,g-1)
    c: Diameter(g5) = 4.5
    c: Equal(g5,g6)
    c: DistanceX(g-1,g5) = 15
    c: DistanceY(g-1,g2) = 35
    c: DistanceX(g5,g6) = 15
    c: DistanceX(g6,g0) = 5
    c: Symmetric(g0,g0,g-1)
    c: DistanceY(g0,g0) = 20
    c: Angle(g3,g4) = 2.35619
FEATURE [PartDesign::Pad] Pad019
  Direction = (1,1,1)
  Length = 5
  Length2 = 100
  Profile = -> Sketch033
  Type = 0
FEATURE [Sketcher::SketchObject] Sketch035
  FullyConstrained = true
  MapMode = 5
  Placement = pos=(0,0,0) rot=(0.57735,0.57735,0.57735;2.0944rad)
  Support = -> [YZ_Plane016]
  expr: Constraints[12] = <<var>>.tensionerJ2ScrewH
  sketch-geometry (7):
    g0: LineSegment StartX=-10 StartY=0 StartZ=0 EndX=35 EndY=0 EndZ=0
    g1: LineSegment StartX=35 StartY=0 StartZ=0 EndX=35 EndY=14.5 EndZ=0
    g2: LineSegment StartX=35 StartY=14.5 StartZ=0 EndX=-10 EndY=14.5 EndZ=0
    g3: LineSegment StartX=-10 StartY=14.5 StartZ=0 EndX=-10 EndY=0 EndZ=0
    g4: Circle CenterX=0 CenterY=9 CenterZ=0 NormalX=0 NormalY=0 NormalZ=1 AngleXU=0 Radius=2.15
    g5: Circle CenterX=0 CenterY=9 CenterZ=0 NormalX=0 NormalY=0 NormalZ=1 AngleXU=0 Radius=3.5
    g6: Circle CenterX=30 CenterY=9 CenterZ=0 NormalX=0 NormalY=0 NormalZ=1 AngleXU=0 Radius=2.15
  constraints (20):
    c: Coincident(g0,g1)
    c: Coincident(g1,g2)
    c: Coincident(g2,g3)
    c: Coincident(g3,g0)
    c: Horizontal(g0)
    c: Vertical(g1)
    c: Vertical(g3)
    c: PointOnObject(g0,g-1)
    c: PointOnObject(g4,g-2)
    c: Diameter(g4) = 4.3
    c: Coincident(g5,g4)
    c: Diameter(g5) = 7
    c: DistanceY(g-1,g4) = 9
    c: DistanceY(g4,g2) = 5.5
    c: DistanceX(g2,g-1) = 10
    c: DistanceX(g-1,g1) = 35
    c: Equal(g6,g4)
    c: Horizontal(g4,g6)
    c: DistanceX(g-1,g6) = 30
    c: Horizontal(g2)
FEATURE [PartDesign::Pad] Pad020
  BaseFeature = -> Pad019
  Direction = (1,1,1)
  Length = 10
  Length2 = 100
  Profile = -> Sketch035
  Type = 0
FEATURE [Sketcher::SketchObject] Sketch102
  AttachmentOffset = pos=(0,0,5) rot=(0,0,1;0rad)
  FullyConstrained = true
  MapMode = 5
  Placement = pos=(0,0,5) rot=(0,0,1;0rad)
  Support = -> [XY_Plane017]
  sketch-geometry (2):
    g0: Circle CenterX=15 CenterY=0 CenterZ=0 NormalX=0 NormalY=0 NormalZ=1 AngleXU=0 Radius=2.25
    g1: Circle CenterX=30 CenterY=0 CenterZ=0 NormalX=0 NormalY=0 NormalZ=1 AngleXU=0 Radius=2.25
  constraints (6):
    c: PointOnObject(g0,g-1)
    c: Diameter(g0) = 4.5
    c: Equal(g0,g1)
    c: DistanceX(g-1,g0) = 15
    c: DistanceX(g0,g1) = 15
    c: PointOnObject(g1,g-1)
FEATURE [PartDesign::Hole] Hole007
  BaseFeature = -> Pad020
  Depth = 25
  DepthType = 1
  Diameter = 4.5
  DrillForDepth = false
  DrillPoint = 1
  DrillPointAngle = 118
  HoleCutCountersinkAngle = 90
  HoleCutCustomValues = false
  HoleCutDepth = 0
  HoleCutDiameter = 9
  HoleCutType = 7
  ModelActualThread = false
  Profile = -> Sketch102
  Refine = true
  Tapered = false
  TaperedAngle = 90
  ThreadAngle = 0
  ThreadClass = 0
  ThreadCutOffInner = 0
  ThreadCutOffOuter = 0
  ThreadDirection = 0
  ThreadFit = 0
  ThreadPitch = 0
  ThreadSize = 11
  ThreadType = 1
  Threaded = false
FEATURE [PartDesign::Body] Body_2
  Group = -> [LCS_0008,Sketch033,Pad019,Sketch035,Pad020,Sketch102,Hole007]
  Origin = -> Origin017
  Tip = -> Hole007
PROVENANCE & LICENSES
A FreeCAD (.FCStd) document from a public repository crawl; recipes are the document's own serialized feature recipes (and, for linked parts, companion documents' recipes).
License: as declared in the source repository (recorded in the dataset sidecar).
